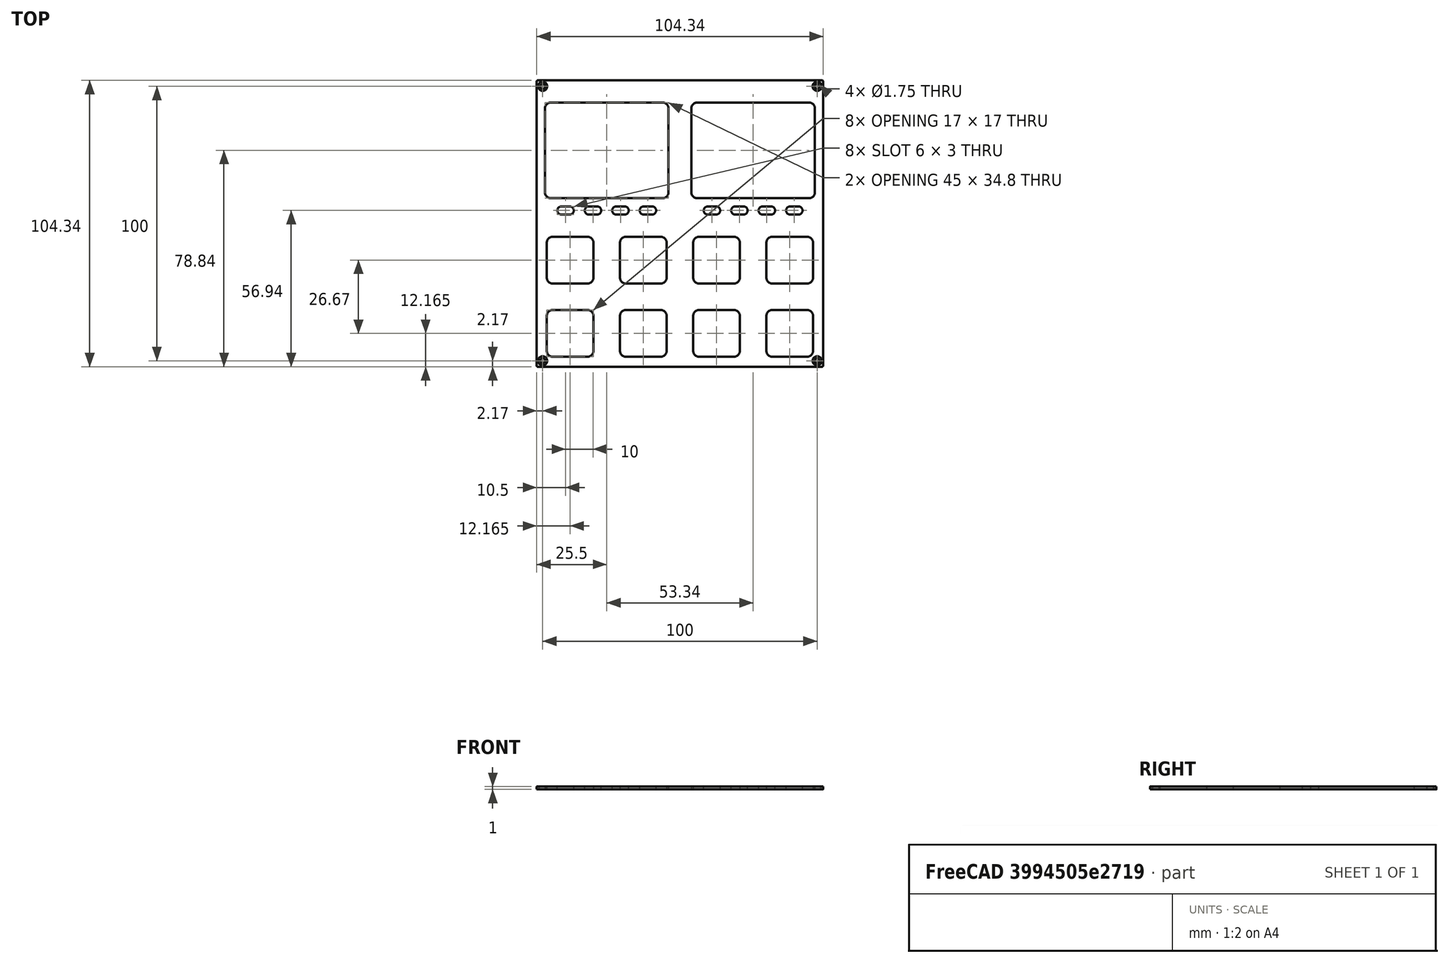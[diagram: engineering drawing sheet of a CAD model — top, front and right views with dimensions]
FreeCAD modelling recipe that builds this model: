
FCSTD DOCUMENT  (FreeCAD 1.0R39109 (Git))
Label: FRONTPANEL-SHEET-VSN2 - button_version1
License: All rights reserved
LicenseURL: https://en.wikipedia.org/wiki/All_rights_reserved
objects: TechDraw::DrawViewDimension×14, Sketcher::SketchObject×11, TechDraw::DrawViewBalloon×11, TechDraw::DrawHatch×11, TechDraw::DrawViewAnnotation×6, TechDraw::DrawViewPart×5, PartDesign::Pocket×4, TechDraw::DrawSVGTemplate×2, PartDesign::Body×2, TechDraw::DrawPage×2, Spreadsheet::Sheet×1, PartDesign::Pad×1, PartDesign::Hole×1, PartDesign::FeatureBase×1, TechDraw::DrawComplexSection×1
note: 65 computed .brp shape members not serialized (recipe doc carries the construction recipe); baked Part::Feature solids carry a one-line shape summary decoded from their .brp

FEATURE [TechDraw::DrawSVGTemplate] Template
  EditableTexts = COLOR=Anodized matte black - RAL code: 9004; CreationDate=2024/08/29; E.G.APPROVED=PRELIMINARY; FC-Scale=1:1; FC-Title=VSN2 - frontpanel; IntechStudioLtd.=Intech Studio Ltd.; MATERIAL=Aluminum 5052-H32; REV=01; STANDARD=ISO 2768 - m
  Height = 297
  Orientation = 1
  Template = <userpath>/Desktop/A3_LandscapeTD_MODIFIED.svg
  Width = 420
FEATURE [Spreadsheet::Sheet] Spreadsheet  label="dim"
  cells = A1='panel_length; B1(panel_length)=104.35; A2='panel_thickness; B2(panel_thickness)=1; A3='panel_radius; B3(panel_radius)==(104.35 - 103.6) / 2; A5='corner_drill_dist; B5(corner_drill_dist)=100; A6='corner_drill_dia; B6(corner_drill_dia)=1.75; A7='corner_drill_countersink; B7(corner_drill_countersink)=3.3; A9='undercut_width; B9(undercut_width)=1; A10='undercut_length; B10(undercut_length)=90; A11='undercut_offset; B11(undercut_offset)=1; A12='undercut_depth; B12(undercut_depth)=0.8; A14='ui_raster; B14(ui_raster)=26.67; A16='light_drill_dia; B16(light_drill_dia)=3; D16='old 2.9; A17='light_bore_dia; B17(light_bore_dia)=3.45; C17='check; D17='old 3.30; E17='DEPRICATED; A18='light_bore_depth; B18(light_bore_depth)=0.4; C18='check; D18='old 0.40; E18='DEPRICATED; A20='pot_drill_dia; B20(pot_drill_dia)=9.8; C20='check; D20='old 6.20; A21='pot_led_dist; B21(pot_led_dist)=8.5; B22=0; A23='but_drill_dia; B23(but_drill_dia)=9.8; A24='but_led_dist; B24(but_led_dist)=8.5; A26='fad_cutout_width; B26(fad_cutout_width)=2.1; C26='check; D26='old 1.50; A27='fad_cutout_length; B27(fad_cutout_length)=36; A28='fad_led_dist; B28(fad_led_dist)=25; A30='enc_drill_dia; B30(enc_drill_dia)=9.8; C30='check; D30='old 6.20; A31='enc_led_dist; B31(enc_led_dist)=8.5; A33='longfad_cutout_width; B33(longfad_cutout_width)=2.1; A34='longfad_cutout_length; B34(longfad_cutout_length)=66; A36='panel_chamfer; B36(panel_chamfer)=0.2; C36='UPDATE DRAWING
FEATURE [Sketcher::SketchObject] Sketch025  label="TEK2_TEKLight"
  ArcFitTolerance = 0
  AttachmentSupport = -> [XY_Plane011]
  FullyConstrained = true
  MakeInternals = false
  MapMode = 5
  expr: Constraints[49] = <<dim>>.light_drill_dia
  sketch-geometry (28):
    g0: Circle [constr] CenterX=-26.67 CenterY=26.67 CenterZ=0 NormalX=0 NormalY=0 NormalZ=1 AngleXU=0 Radius=5.25
    g1: Circle CenterX=26.67 CenterY=26.67 CenterZ=0 NormalX=0 NormalY=0 NormalZ=1 AngleXU=0 Radius=5.25
    g2: LineSegment [constr] StartX=-26.67 StartY=26.67 StartZ=0 EndX=0 EndY=26.67 EndZ=0
    g3: LineSegment [constr] StartX=0 StartY=26.67 StartZ=0 EndX=0 EndY=0 EndZ=0
    g4: LineSegment [constr] StartX=26.67 StartY=26.67 StartZ=0 EndX=0 EndY=26.67 EndZ=0
    g5: Circle [constr] CenterX=-26.67 CenterY=26.67 CenterZ=0 NormalX=0 NormalY=0 NormalZ=1 AngleXU=0 Radius=23
    g6: Circle [constr] CenterX=26.67 CenterY=26.67 CenterZ=0 NormalX=0 NormalY=0 NormalZ=1 AngleXU=0 Radius=23
    g7: Circle [constr] CenterX=-47.5151 CenterY=36.3902 CenterZ=0 NormalX=0 NormalY=0 NormalZ=1 AngleXU=0 Radius=1.5
    g8: Circle [constr] CenterX=-45.5105 CenterY=39.8623 CenterZ=0 NormalX=0 NormalY=0 NormalZ=1 AngleXU=0 Radius=1.5
    g9: Circle [constr] CenterX=-42.9335 CenterY=42.9335 CenterZ=0 NormalX=0 NormalY=0 NormalZ=1 AngleXU=0 Radius=1.5
    g10: Circle [constr] CenterX=-39.8623 CenterY=45.5105 CenterZ=0 NormalX=0 NormalY=0 NormalZ=1 AngleXU=0 Radius=1.5
    g11: Circle [constr] CenterX=-36.3902 CenterY=47.5151 CenterZ=0 NormalX=0 NormalY=0 NormalZ=1 AngleXU=0 Radius=1.5
    g12: Circle CenterX=5.82492 CenterY=36.3902 CenterZ=0 NormalX=0 NormalY=0 NormalZ=1 AngleXU=0 Radius=1.5
    g13: Circle CenterX=7.8295 CenterY=39.8623 CenterZ=0 NormalX=0 NormalY=0 NormalZ=1 AngleXU=0 Radius=1.5
    g14: Circle CenterX=10.4065 CenterY=42.9335 CenterZ=0 NormalX=0 NormalY=0 NormalZ=1 AngleXU=0 Radius=1.5
    g15: Circle CenterX=13.4777 CenterY=45.5105 CenterZ=0 NormalX=0 NormalY=0 NormalZ=1 AngleXU=0 Radius=1.5
    g16: Circle CenterX=16.9498 CenterY=47.5151 CenterZ=0 NormalX=0 NormalY=0 NormalZ=1 AngleXU=0 Radius=1.5
    g17: LineSegment [constr] StartX=-47.5151 StartY=36.3902 StartZ=0 EndX=5.82492 EndY=36.3902 EndZ=0
    g18: LineSegment [constr] StartX=-45.5105 StartY=39.8623 StartZ=0 EndX=7.8295 EndY=39.8623 EndZ=0
    g19: LineSegment [constr] StartX=-42.9335 StartY=42.9335 StartZ=0 EndX=10.4065 EndY=42.9335 EndZ=0
    g20: LineSegment [constr] StartX=-39.8623 StartY=45.5105 StartZ=0 EndX=13.4777 EndY=45.5105 EndZ=0
    g21: LineSegment [constr] StartX=-36.3902 StartY=47.5151 StartZ=0 EndX=16.9498 EndY=47.5151 EndZ=0
    g22: LineSegment [constr] StartX=5.82492 StartY=36.3902 StartZ=0 EndX=26.67 EndY=26.67 EndZ=0
    g23: LineSegment [constr] StartX=16.9498 StartY=47.5151 StartZ=0 EndX=26.67 EndY=26.67 EndZ=0
    g24: LineSegment [constr] StartX=5.82492 StartY=36.3902 StartZ=0 EndX=7.8295 EndY=39.8623 EndZ=0
    g25: LineSegment [constr] StartX=7.8295 StartY=39.8623 StartZ=0 EndX=10.4065 EndY=42.9335 EndZ=0
    g26: LineSegment [constr] StartX=13.4777 StartY=45.5105 StartZ=0 EndX=10.4065 EndY=42.9335 EndZ=0
    g27: LineSegment [constr] StartX=16.9498 StartY=47.5151 StartZ=0 EndX=13.4777 EndY=45.5105 EndZ=0
  constraints (69):
    c: Coincident(g2,g0)
    c: PointOnObject(g2,g-2)
    c: Coincident(g2,g3)
    c: Coincident(g3,g-1)
    c: Coincident(g4,g1)
    c: Coincident(g4,g2)
    c: Equal(g3,g2)
    c: Equal(g2,g4)
    c: Horizontal(g2)
    c: Horizontal(g4)
    c: DistanceY(g3,g3) = 26.67
    c: Equal(g0,g1)
    c: Coincident(g5,g0)
    c: Coincident(g6,g1)
    c: Equal(g6,g5)
    c: PointOnObject(g7,g5)
    c: PointOnObject(g8,g5)
    c: PointOnObject(g9,g5)
    c: PointOnObject(g10,g5)
    c: PointOnObject(g11,g5)
    c: PointOnObject(g12,g6)
    c: PointOnObject(g13,g6)
    c: PointOnObject(g14,g6)
    c: PointOnObject(g15,g6)
    c: PointOnObject(g16,g6)
    c: Equal(g7,g8)
    c: Equal(g8,g9)
    c: Equal(g9,g10)
    c: Equal(g10,g11)
    c: Equal(g11,g12)
    c: Equal(g12,g13)
    c: Equal(g13,g14)
    c: Equal(g14,g15)
    c: Equal(g15,g16)
    c: Coincident(g17,g7)
    c: Coincident(g17,g12)
    c: Coincident(g18,g8)
    c: Coincident(g18,g13)
    c: Horizontal(g18)
    c: Coincident(g19,g9)
    c: Coincident(g19,g14)
    c: Horizontal(g19)
    c: Coincident(g20,g10)
    c: Coincident(g20,g15)
    c: Horizontal(g20)
    c: Coincident(g21,g11)
    c: Horizontal(g21)
    c: Coincident(g21,g16)
    c: Horizontal(g17)
    c: Diameter(g12) = 3
    c: Coincident(g22,g12)
    c: Coincident(g22,g1)
    c: Coincident(g23,g16)
    c: Coincident(g23,g1)
    c: Angle(g22,g4) = 0.436332
    c: Angle(g-2,g23) = 0.436332
    c: Coincident(g24,g12)
    c: Coincident(g24,g13)
    c: Coincident(g25,g13)
    c: Coincident(g26,g15)
    c: Coincident(g26,g25)
    c: Coincident(g27,g16)
    c: Coincident(g27,g15)
    c: Coincident(g25,g14)
    c: Equal(g24,g25)
    c: Equal(g25,g26)
    c: Equal(g26,g27)
    c: Radius(g6) = 23
    c: Diameter(g1) = 10.5
FEATURE [Sketcher::SketchObject] Sketch024  label="TEK2_ButtonLight"
  ArcFitTolerance = 0
  AttachmentSupport = -> [XY_Plane011]
  FullyConstrained = true
  MakeInternals = false
  MapMode = 5
  expr: Constraints[42] = <<dim>>.but_led_dist
  sketch-geometry (17):
    g0: Circle CenterX=-40.005 CenterY=-4.835 CenterZ=0 NormalX=0 NormalY=0 NormalZ=1 AngleXU=0 Radius=2
    g1: Circle CenterX=-13.335 CenterY=-4.835 CenterZ=0 NormalX=0 NormalY=0 NormalZ=1 AngleXU=0 Radius=2
    g2: LineSegment [constr] StartX=-40.005 StartY=-4.835 StartZ=0 EndX=-13.335 EndY=-4.835 EndZ=0
    g3: Circle CenterX=13.335 CenterY=-4.835 CenterZ=0 NormalX=0 NormalY=0 NormalZ=1 AngleXU=0 Radius=2
    g4: LineSegment [constr] StartX=-13.335 StartY=-4.835 StartZ=0 EndX=13.335 EndY=-4.835 EndZ=0
    g5: Circle CenterX=40.005 CenterY=-4.835 CenterZ=0 NormalX=0 NormalY=0 NormalZ=1 AngleXU=0 Radius=2
    g6: LineSegment [constr] StartX=13.335 StartY=-4.835 StartZ=0 EndX=40.005 EndY=-4.835 EndZ=0
    g7: Circle CenterX=-40.005 CenterY=-31.505 CenterZ=0 NormalX=0 NormalY=0 NormalZ=1 AngleXU=0 Radius=2
    g8: LineSegment [constr] StartX=-40.005 StartY=-4.835 StartZ=0 EndX=-40.005 EndY=-31.505 EndZ=0
    g9: Circle CenterX=-13.335 CenterY=-31.505 CenterZ=0 NormalX=0 NormalY=0 NormalZ=1 AngleXU=0 Radius=2
    g10: LineSegment [constr] StartX=-40.005 StartY=-31.505 StartZ=0 EndX=-13.335 EndY=-31.505 EndZ=0
    g11: Circle CenterX=13.335 CenterY=-31.505 CenterZ=0 NormalX=0 NormalY=0 NormalZ=1 AngleXU=0 Radius=2
    g12: LineSegment [constr] StartX=-13.335 StartY=-31.505 StartZ=0 EndX=13.335 EndY=-31.505 EndZ=0
    g13: Circle CenterX=40.005 CenterY=-31.505 CenterZ=0 NormalX=0 NormalY=0 NormalZ=1 AngleXU=0 Radius=2
    g14: LineSegment [constr] StartX=13.335 StartY=-31.505 StartZ=0 EndX=40.005 EndY=-31.505 EndZ=0
    g15: LineSegment [constr] StartX=-13.335 StartY=-4.835 StartZ=0 EndX=-1.8e-15 EndY=8.5 EndZ=0
    g16: LineSegment [constr] StartX=-1.8e-15 StartY=8.5 StartZ=0 EndX=13.335 EndY=-4.835 EndZ=0
  constraints (43):
    c: Diameter(g0) = 4
    c: Coincident(g0,g2)
    c: Coincident(g1,g2)
    c: Coincident(g1,g4)
    c: Coincident(g3,g4)
    c: Coincident(g3,g6)
    c: Coincident(g5,g6)
    c: Coincident(g0,g8)
    c: Coincident(g7,g8)
    c: Coincident(g7,g10)
    c: Coincident(g9,g10)
    c: Coincident(g9,g12)
    c: Coincident(g11,g12)
    c: Coincident(g11,g14)
    c: Coincident(g13,g14)
    c: Horizontal(g4)
    c: Horizontal(g2)
    c: Horizontal(g6)
    c: Horizontal(g10)
    c: Horizontal(g12)
    c: Horizontal(g14)
    c: Vertical(g8)
    c: Equal(g8,g2)
    c: Equal(g2,g10)
    c: Equal(g10,g12)
    c: Equal(g12,g4)
    c: Equal(g4,g6)
    c: Equal(g6,g14)
    c: DistanceX(g4,g4) = 26.67
    c: Equal(g7,g9)
    c: Equal(g9,g11)
    c: Equal(g11,g13)
    c: Equal(g13,g5)
    c: Equal(g5,g3)
    c: Equal(g3,g1)
    c: Equal(g1,g0)
    c: Coincident(g15,g1)
    c: PointOnObject(g15,g-2)
    c: Coincident(g15,g16)
    c: Coincident(g16,g3)
    c: Equal(g16,g15)
    c: Perpendicular(g15,g16)
    c: DistanceY(g-1,g15) = 8.5
FEATURE [Sketcher::SketchObject] Sketch023  label="TEK2_ButtonHole"
  ArcFitTolerance = 0
  AttachmentSupport = -> [XY_Plane011]
  FullyConstrained = true
  MakeInternals = false
  MapMode = 5
  sketch-geometry (17):
    g0: Circle CenterX=-40.005 CenterY=-13.335 CenterZ=0 NormalX=0 NormalY=0 NormalZ=1 AngleXU=0 Radius=2
    g1: Circle CenterX=-13.335 CenterY=-13.335 CenterZ=0 NormalX=0 NormalY=0 NormalZ=1 AngleXU=0 Radius=2
    g2: LineSegment [constr] StartX=-40.005 StartY=-13.335 StartZ=0 EndX=-13.335 EndY=-13.335 EndZ=0
    g3: Circle CenterX=13.335 CenterY=-13.335 CenterZ=0 NormalX=0 NormalY=0 NormalZ=1 AngleXU=0 Radius=2
    g4: LineSegment [constr] StartX=-13.335 StartY=-13.335 StartZ=0 EndX=13.335 EndY=-13.335 EndZ=0
    g5: Circle CenterX=40.005 CenterY=-13.335 CenterZ=0 NormalX=0 NormalY=0 NormalZ=1 AngleXU=0 Radius=2
    g6: LineSegment [constr] StartX=13.335 StartY=-13.335 StartZ=0 EndX=40.005 EndY=-13.335 EndZ=0
    g7: Circle CenterX=-40.005 CenterY=-40.005 CenterZ=0 NormalX=0 NormalY=0 NormalZ=1 AngleXU=0 Radius=2
    g8: LineSegment [constr] StartX=-40.005 StartY=-13.335 StartZ=0 EndX=-40.005 EndY=-40.005 EndZ=0
    g9: Circle CenterX=-13.335 CenterY=-40.005 CenterZ=0 NormalX=0 NormalY=0 NormalZ=1 AngleXU=0 Radius=2
    g10: LineSegment [constr] StartX=-40.005 StartY=-40.005 StartZ=0 EndX=-13.335 EndY=-40.005 EndZ=0
    g11: Circle CenterX=13.335 CenterY=-40.005 CenterZ=0 NormalX=0 NormalY=0 NormalZ=1 AngleXU=0 Radius=2
    g12: LineSegment [constr] StartX=-13.335 StartY=-40.005 StartZ=0 EndX=13.335 EndY=-40.005 EndZ=0
    g13: Circle CenterX=40.005 CenterY=-40.005 CenterZ=0 NormalX=0 NormalY=0 NormalZ=1 AngleXU=0 Radius=2
    g14: LineSegment [constr] StartX=13.335 StartY=-40.005 StartZ=0 EndX=40.005 EndY=-40.005 EndZ=0
    g15: LineSegment [constr] StartX=0 StartY=0 StartZ=0 EndX=13.335 EndY=-13.335 EndZ=0
    g16: LineSegment [constr] StartX=0 StartY=0 StartZ=0 EndX=-13.335 EndY=-13.335 EndZ=0
  constraints (42):
    c: Diameter(g0) = 4
    c: Coincident(g0,g2)
    c: Coincident(g1,g2)
    c: Coincident(g1,g4)
    c: Coincident(g3,g4)
    c: Coincident(g3,g6)
    c: Coincident(g5,g6)
    c: Coincident(g0,g8)
    c: Coincident(g7,g8)
    c: Coincident(g7,g10)
    c: Coincident(g9,g10)
    c: Coincident(g9,g12)
    c: Coincident(g11,g12)
    c: Coincident(g11,g14)
    c: Coincident(g13,g14)
    c: Coincident(g-1,g16)
    c: Coincident(g16,g1)
    c: Coincident(g15,g3)
    c: Horizontal(g4)
    c: Horizontal(g2)
    c: Horizontal(g6)
    c: Horizontal(g10)
    c: Horizontal(g12)
    c: Horizontal(g14)
    c: Vertical(g8)
    c: Equal(g8,g2)
    c: Equal(g2,g10)
    c: Equal(g10,g12)
    c: Equal(g12,g4)
    c: Equal(g4,g6)
    c: Equal(g6,g14)
    c: DistanceX(g4,g4) = 26.67
    c: Equal(g16,g15)
    c: Coincident(g15,g16)
    c: Perpendicular(g15,g16)
    c: Equal(g7,g9)
    c: Equal(g9,g11)
    c: Equal(g11,g13)
    c: Equal(g13,g5)
    c: Equal(g5,g3)
    c: Equal(g3,g1)
    c: Equal(g1,g0)
FEATURE [Sketcher::SketchObject] Sketch001
  ArcFitTolerance = 0
  AttachmentSupport = -> [XY_Plane]
  FullyConstrained = true
  MakeInternals = false
  MapMode = 5
  expr: Constraints[13] = <<dim>>.corner_drill_dist
  sketch-geometry (9):
    g0: LineSegment [constr] StartX=-50 StartY=50 StartZ=0 EndX=-50 EndY=-50 EndZ=0
    g1: LineSegment [constr] StartX=-50 StartY=-50 StartZ=0 EndX=50 EndY=-50 EndZ=0
    g2: LineSegment [constr] StartX=50 StartY=-50 StartZ=0 EndX=50 EndY=50 EndZ=0
    g3: LineSegment [constr] StartX=50 StartY=50 StartZ=0 EndX=-50 EndY=50 EndZ=0
    g4: Circle [constr] CenterX=0 CenterY=0 CenterZ=0 NormalX=0 NormalY=0 NormalZ=1 AngleXU=0 Radius=70.7107
    g5: Circle CenterX=-50 CenterY=50 CenterZ=0 NormalX=0 NormalY=0 NormalZ=1 AngleXU=0 Radius=0.5
    g6: Circle CenterX=50 CenterY=50 CenterZ=0 NormalX=0 NormalY=0 NormalZ=1 AngleXU=0 Radius=0.5
    g7: Circle CenterX=50 CenterY=-50 CenterZ=0 NormalX=0 NormalY=0 NormalZ=1 AngleXU=0 Radius=0.5
    g8: Circle CenterX=-50 CenterY=-50 CenterZ=0 NormalX=0 NormalY=0 NormalZ=1 AngleXU=0 Radius=0.5
  constraints (22):
    c: Coincident(g0,g1)
    c: Coincident(g1,g2)
    c: Coincident(g2,g3)
    c: Coincident(g3,g0)
    c: Equal(g0,g1)
    c: Equal(g0,g2)
    c: Equal(g0,g3)
    c: PointOnObject(g0,g4)
    c: PointOnObject(g1,g4)
    c: PointOnObject(g2,g4)
    c: PointOnObject(g3,g4)
    c: Coincident(g4,g-1)
    c: Horizontal(g3)
    c: DistanceX(g3,g3) = 100
    c: Coincident(g5,g0)
    c: Coincident(g6,g2)
    c: Coincident(g7,g1)
    c: Coincident(g8,g0)
    c: Diameter(g8) = 1
    c: Equal(g8,g7)
    c: Equal(g8,g6)
    c: Equal(g8,g5)
FEATURE [Sketcher::SketchObject] Sketch002
  ArcFitTolerance = 0
  AttachmentOffset = pos=(0,0,-4.8) rot=(0,0,1;0rad)
  AttachmentSupport = -> [XY_Plane]
  FullyConstrained = true
  MakeInternals = false
  MapMode = 5
  Placement = pos=(0,0,-4.8) rot=(0,0,1;0rad)
  expr: .AttachmentOffset.Base.z = -<<dim>>.undercut_depth - 4
  expr: Constraints[91] = <<dim>>.undercut_length
  expr: Constraints[92] = <<dim>>.undercut_width
  expr: Constraints[93] = <<dim>>.panel_length / 2 - <<dim>>.undercut_offset - <<dim>>.undercut_width / 2
  sketch-geometry (40):
    g0: LineSegment StartX=-45 StartY=50.175 StartZ=0 EndX=45 EndY=50.175 EndZ=0
    g1: LineSegment StartX=-45 StartY=51.175 StartZ=0 EndX=45 EndY=51.175 EndZ=0
    g2: LineSegment [constr] StartX=-50.675 StartY=45 StartZ=0 EndX=0 EndY=0 EndZ=0
    g3: LineSegment [constr] StartX=0 StartY=0 StartZ=0 EndX=-50.675 EndY=-45 EndZ=0
    g4: LineSegment [constr] StartX=0 StartY=0 StartZ=0 EndX=-45 EndY=50.675 EndZ=0
    g5: LineSegment [constr] StartX=45 StartY=50.675 StartZ=0 EndX=0 EndY=0 EndZ=0
    g6: LineSegment [constr] StartX=0 StartY=0 StartZ=0 EndX=50.675 EndY=45 EndZ=0
    g7: LineSegment [constr] StartX=50.675 StartY=-45 StartZ=0 EndX=0 EndY=0 EndZ=0
    g8: LineSegment [constr] StartX=0 StartY=0 StartZ=0 EndX=45 EndY=-50.675 EndZ=0
    g9: LineSegment [constr] StartX=0 StartY=0 StartZ=0 EndX=-45 EndY=-50.675 EndZ=0
    g10: ArcOfCircle CenterX=45 CenterY=50.675 CenterZ=0 NormalX=0 NormalY=0 NormalZ=1 AngleXU=0 Radius=0.5 StartAngle=4.71239 EndAngle=6.28319
    g11: ArcOfCircle CenterX=45 CenterY=50.675 CenterZ=0 NormalX=0 NormalY=0 NormalZ=1 AngleXU=0 Radius=0.5 StartAngle=0 EndAngle=1.5708
    g12: LineSegment [constr] StartX=45 StartY=50.675 StartZ=0 EndX=45.5 EndY=50.675 EndZ=0
    g13: ArcOfCircle CenterX=-45 CenterY=50.675 CenterZ=0 NormalX=0 NormalY=0 NormalZ=1 AngleXU=0 Radius=0.5 StartAngle=3.14159 EndAngle=4.71239
    g14: ArcOfCircle CenterX=-45 CenterY=50.675 CenterZ=0 NormalX=0 NormalY=0 NormalZ=1 AngleXU=0 Radius=0.5 StartAngle=1.5708 EndAngle=3.14159
    g15: LineSegment [constr] StartX=-45.5 StartY=50.675 StartZ=0 EndX=-45 EndY=50.675 EndZ=0
    g16: LineSegment StartX=-45 StartY=-51.175 StartZ=0 EndX=45 EndY=-51.175 EndZ=0
    g17: LineSegment StartX=-45 StartY=-50.175 StartZ=0 EndX=45 EndY=-50.175 EndZ=0
    g18: ArcOfCircle CenterX=45 CenterY=-50.675 CenterZ=0 NormalX=0 NormalY=0 NormalZ=1 AngleXU=0 Radius=0.5 StartAngle=4.71239 EndAngle=6.28319
    g19: ArcOfCircle CenterX=45 CenterY=-50.675 CenterZ=0 NormalX=0 NormalY=0 NormalZ=1 AngleXU=0 Radius=0.5 StartAngle=0 EndAngle=1.5708
    g20: LineSegment [constr] StartX=45 StartY=-50.675 StartZ=0 EndX=45.5 EndY=-50.675 EndZ=0
    g21: ArcOfCircle CenterX=-45 CenterY=-50.675 CenterZ=0 NormalX=0 NormalY=0 NormalZ=1 AngleXU=0 Radius=0.5 StartAngle=3.14159 EndAngle=4.71239
    g22: ArcOfCircle CenterX=-45 CenterY=-50.675 CenterZ=0 NormalX=0 NormalY=0 NormalZ=1 AngleXU=0 Radius=0.5 StartAngle=1.5708 EndAngle=3.14159
    g23: LineSegment [constr] StartX=-45.5 StartY=-50.675 StartZ=0 EndX=-45 EndY=-50.675 EndZ=0
    g24: LineSegment StartX=51.175 StartY=-45 StartZ=0 EndX=51.175 EndY=45 EndZ=0
    g25: LineSegment StartX=50.175 StartY=-45 StartZ=0 EndX=50.175 EndY=45 EndZ=0
    g26: ArcOfCircle CenterX=50.675 CenterY=45 CenterZ=0 NormalX=0 NormalY=0 NormalZ=1 AngleXU=0 Radius=0.5 StartAngle=3.8e-15 EndAngle=1.5708
    g27: ArcOfCircle CenterX=50.675 CenterY=45 CenterZ=0 NormalX=0 NormalY=0 NormalZ=1 AngleXU=0 Radius=0.5 StartAngle=1.5708 EndAngle=3.14159
    g28: LineSegment [constr] StartX=50.675 StartY=45 StartZ=0 EndX=50.675 EndY=45.5 EndZ=0
    g29: ArcOfCircle CenterX=50.675 CenterY=-45 CenterZ=0 NormalX=0 NormalY=0 NormalZ=1 AngleXU=0 Radius=0.5 StartAngle=4.71239 EndAngle=6.28319
    g30: ArcOfCircle CenterX=50.675 CenterY=-45 CenterZ=0 NormalX=0 NormalY=0 NormalZ=1 AngleXU=0 Radius=0.5 StartAngle=3.14159 EndAngle=4.71239
    g31: LineSegment [constr] StartX=50.675 StartY=-45.5 StartZ=0 EndX=50.675 EndY=-45 EndZ=0
    g32: LineSegment StartX=-50.175 StartY=-45 StartZ=0 EndX=-50.175 EndY=45 EndZ=0
    g33: LineSegment StartX=-51.175 StartY=-45 StartZ=0 EndX=-51.175 EndY=45 EndZ=0
    g34: ArcOfCircle CenterX=-50.675 CenterY=45 CenterZ=0 NormalX=0 NormalY=0 NormalZ=1 AngleXU=0 Radius=0.5 StartAngle=1.4e-15 EndAngle=1.5708
    g35: ArcOfCircle CenterX=-50.675 CenterY=45 CenterZ=0 NormalX=0 NormalY=0 NormalZ=1 AngleXU=0 Radius=0.5 StartAngle=1.5708 EndAngle=3.14159
    g36: LineSegment [constr] StartX=-50.675 StartY=45 StartZ=0 EndX=-50.675 EndY=45.5 EndZ=0
    g37: ArcOfCircle CenterX=-50.675 CenterY=-45 CenterZ=0 NormalX=0 NormalY=0 NormalZ=1 AngleXU=0 Radius=0.5 StartAngle=4.71239 EndAngle=6.28319
    g38: ArcOfCircle CenterX=-50.675 CenterY=-45 CenterZ=0 NormalX=0 NormalY=0 NormalZ=1 AngleXU=0 Radius=0.5 StartAngle=3.14159 EndAngle=4.71239
    g39: LineSegment [constr] StartX=-50.675 StartY=-45.5 StartZ=0 EndX=-50.675 EndY=-45 EndZ=0
  constraints (96):
    c: Horizontal(g0)
    c: Coincident(g2,g-1)
    c: Coincident(g2,g3)
    c: Coincident(g-1,g4)
    c: Coincident(g5,g-1)
    c: Coincident(g5,g6)
    c: Coincident(g7,g-1)
    c: Coincident(g7,g8)
    c: Coincident(g-1,g9)
    c: Equal(g5,g6)
    c: Equal(g6,g8)
    c: Equal(g8,g7)
    c: Equal(g7,g9)
    c: Equal(g9,g3)
    c: Equal(g3,g2)
    c: Equal(g2,g4)
    c: Coincident(g10,g5)
    c: Coincident(g11,g10)
    c: Coincident(g11,g10)
    c: Tangent(g11,g1) = 1.5708
    c: Tangent(g10,g0) = -1.5708
    c: Coincident(g12,g10)
    c: Coincident(g12,g10)
    c: Horizontal(g12)
    c: Coincident(g13,g4)
    c: Coincident(g14,g13)
    c: Coincident(g14,g13)
    c: Tangent(g14,g1) = 1.5708
    c: Tangent(g13,g0) = -1.5708
    c: Coincident(g15,g13)
    c: Coincident(g15,g13)
    c: Horizontal(g15)
    c: Horizontal(g1)
    c: Horizontal(g16)
    c: Coincident(g19,g18)
    c: Coincident(g19,g18)
    c: Tangent(g19,g17) = 1.5708
    c: Tangent(g18,g16) = -1.5708
    c: Coincident(g20,g18)
    c: Coincident(g20,g18)
    c: Horizontal(g20)
    c: Coincident(g22,g21)
    c: Coincident(g22,g21)
    c: Tangent(g22,g17) = 1.5708
    c: Tangent(g21,g16) = -1.5708
    c: Coincident(g23,g21)
    c: Coincident(g23,g21)
    c: Horizontal(g23)
    c: Horizontal(g17)
    c: Coincident(g21,g9)
    c: Coincident(g8,g18)
    c: Equal(g22,g14)
    c: Equal(g17,g1)
    c: Coincident(g27,g26)
    c: Coincident(g27,g26)
    c: Tangent(g27,g25) = 1.5708
    c: Tangent(g26,g24) = -1.5708
    c: Coincident(g28,g26)
    c: Coincident(g28,g26)
    c: Coincident(g30,g29)
    c: Coincident(g30,g29)
    c: Tangent(g30,g25) = 1.5708
    c: Tangent(g29,g24) = -1.5708
    c: Coincident(g31,g29)
    c: Coincident(g31,g29)
    c: Vertical(g31)
    c: Vertical(g28)
    c: Vertical(g25)
    c: Vertical(g24)
    c: Coincident(g35,g34)
    c: Coincident(g35,g34)
    c: Tangent(g35,g33) = 1.5708
    c: Tangent(g34,g32) = -1.5708
    c: Coincident(g36,g34)
    c: Coincident(g36,g34)
    c: Coincident(g38,g37)
    c: Coincident(g38,g37)
    c: Tangent(g38,g33) = 1.5708
    c: Tangent(g37,g32) = -1.5708
    c: Coincident(g39,g37)
    c: Coincident(g39,g37)
    c: Vertical(g39)
    c: Vertical(g36)
    c: Vertical(g33)
    c: Vertical(g32)
    c: Coincident(g6,g26)
    c: Coincident(g7,g29)
    c: Equal(g25,g0)
    c: Equal(g11,g27)
    c: Equal(g1,g33)
    c: Equal(g35,g11)
    c: DistanceX(g13,g10) = 90
    c: Diameter(g13) = 1
    c: DistanceY(g-1,g13) = 50.675
    c: Coincident(g2,g34)
    c: Coincident(g3,g37)
FEATURE [Sketcher::SketchObject] Sketch
  ArcFitTolerance = 0
  AttachmentSupport = -> [XY_Plane]
  FullyConstrained = true
  MakeInternals = false
  MapMode = 5
  expr: Constraints[12] = <<dim>>.panel_radius
  expr: Constraints[16] = <<dim>>.panel_length
  sketch-geometry (11):
    g0: LineSegment StartX=-51.8 StartY=52.175 StartZ=0 EndX=51.8 EndY=52.175 EndZ=0
    g1: LineSegment StartX=52.175 StartY=51.8 StartZ=0 EndX=52.175 EndY=-51.8 EndZ=0
    g2: LineSegment StartX=51.8 StartY=-52.175 StartZ=0 EndX=-51.8 EndY=-52.175 EndZ=0
    g3: LineSegment StartX=-52.175 StartY=-51.8 StartZ=0 EndX=-52.175 EndY=51.8 EndZ=0
    g4: ArcOfCircle CenterX=-51.8 CenterY=51.8 CenterZ=0 NormalX=0 NormalY=0 NormalZ=1 AngleXU=0 Radius=0.375 StartAngle=1.5708 EndAngle=3.14159
    g5: ArcOfCircle CenterX=51.8 CenterY=51.8 CenterZ=0 NormalX=0 NormalY=0 NormalZ=1 AngleXU=0 Radius=0.375 StartAngle=8.4e-15 EndAngle=1.5708
    g6: ArcOfCircle CenterX=51.8 CenterY=-51.8 CenterZ=0 NormalX=0 NormalY=0 NormalZ=1 AngleXU=0 Radius=0.375 StartAngle=4.71239 EndAngle=6.28319
    g7: ArcOfCircle CenterX=-51.8 CenterY=-51.8 CenterZ=0 NormalX=0 NormalY=0 NormalZ=1 AngleXU=0 Radius=0.375 StartAngle=3.14159 EndAngle=4.71239
    g8: LineSegment [constr] StartX=-51.8 StartY=51.8 StartZ=0 EndX=0 EndY=0 EndZ=0
    g9: LineSegment [constr] StartX=0 StartY=0 StartZ=0 EndX=51.8 EndY=51.8 EndZ=0
    g10: LineSegment [constr] StartX=0 StartY=0 StartZ=0 EndX=-51.8 EndY=-51.8 EndZ=0
  constraints (26):
    c: Horizontal(g0)
    c: Horizontal(g2)
    c: Vertical(g1)
    c: Vertical(g3)
    c: Tangent(g3,g4) = 1.5708
    c: Tangent(g0,g4) = 1.5708
    c: Tangent(g0,g5) = 1.5708
    c: Tangent(g1,g5) = 1.5708
    c: Tangent(g1,g6) = 1.5708
    c: Tangent(g2,g6) = 1.5708
    c: Tangent(g2,g7) = 1.5708
    c: Tangent(g3,g7) = 1.5708
    c: Radius(g4) = 0.375
    c: Equal(g4,g5)
    c: Equal(g4,g6)
    c: Equal(g4,g7)
    c: DistanceX(g3,g1) = 104.35
    c: Equal(g3,g0)
    c: Coincident(g8,g4)
    c: Coincident(g8,g-1)
    c: Coincident(g8,g9)
    c: Coincident(g9,g5)
    c: Coincident(g-1,g10)
    c: Coincident(g10,g7)
    c: Equal(g10,g8)
    c: Equal(g8,g9)
FEATURE [PartDesign::Pad] Pad  label="panel"
  AllowMultiFace = false
  Direction = (0,0,1)
  Length = 1
  Length2 = 100
  Profile = -> Sketch
  Reversed = true
  Suppressed = false
  Type = 0
  expr: Length = <<dim>>.panel_thickness
FEATURE [PartDesign::Pocket] Pocket
  AllowMultiFace = false
  BaseFeature = -> Pad
  Direction = (0,0,-1)
  Length = 5
  Length2 = 100
  Profile = -> Sketch002
  Suppressed = false
  Type = 1
FEATURE [PartDesign::Hole] Hole
  BaseFeature = -> Pocket
  CustomThreadClearance = 0
  Depth = 298.105
  DepthType = 1
  Diameter = 1.75
  DrillForDepth = false
  DrillPoint = 1
  DrillPointAngle = 118
  HoleCutCountersinkAngle = 90
  HoleCutCustomValues = false
  HoleCutDepth = 0
  HoleCutDiameter = 3.3
  HoleCutType = 2
  ModelThread = false
  Profile = -> Sketch001
  Suppressed = false
  Tapered = false
  TaperedAngle = 90
  ThreadClass = 0
  ThreadDepth = 298.105
  ThreadDepthType = 0
  ThreadDirection = 0
  ThreadFit = 0
  ThreadSize = 0
  ThreadType = 0
  Threaded = false
  UseCustomThreadClearance = false
  expr: Diameter = <<dim>>.corner_drill_dia
  expr: HoleCutDiameter = <<dim>>.corner_drill_countersink
FEATURE [PartDesign::Body] Body  label="Base"
  AllowCompound = false
  Group = -> [Sketch,Pad,Sketch001,Sketch002,Pocket,Hole]
  Origin = -> Origin
  Tip = -> Hole
FEATURE [PartDesign::FeatureBase] Clone009
  BaseFeature = -> Body
  Suppressed = false
FEATURE [Sketcher::SketchObject] Sketch026  label="Section A-A"
  ArcFitTolerance = 0
  AttachmentSupport = -> [XY_Plane011]
  FullyConstrained = true
  MakeInternals = false
  MapMode = 5
  sketch-geometry (1):
    g0: LineSegment StartX=-53.5 StartY=-50 StartZ=0 EndX=-46.5 EndY=-50 EndZ=0
  constraints (4):
    c: Horizontal(g0)
    c: DistanceX(g0,g0) = 7
    c: DistanceY(g0,g-1) = 50
    c: DistanceX(g0,g-1) = 46.5
FEATURE [TechDraw::DrawViewAnnotation] Annotation
  Font = osifont
  LineSpace = 100
  LockPosition = false
  MaxWidth = -1
  Rotation = 0
  ScaleType = 0
  Text = 10:1
  TextSize = 4
  TextStyle = 0
  X = 287.429
  Y = 78.3445
FEATURE [TechDraw::DrawViewAnnotation] Annotation001
  Font = osifont
  LineSpace = 100
  LockPosition = false
  MaxWidth = -1
  Rotation = 0
  ScaleType = 0
  Text = 1:2
  TextSize = 4
  TextStyle = 0
  X = 191.608
  Y = 62.7873
FEATURE [Sketcher::SketchObject] Sketch027
  ArcFitTolerance = 0
  AttachmentSupport = -> [XY_Plane011]
  FullyConstrained = true
  MakeInternals = false
  MapMode = 5
  sketch-geometry (19):
    g0: LineSegment StartX=-49.17 StartY=11.27 StartZ=0 EndX=-49.17 EndY=42.07 EndZ=0
    g1: LineSegment StartX=-47.17 StartY=44.07 StartZ=0 EndX=-6.17 EndY=44.07 EndZ=0
    g2: LineSegment StartX=-4.17 StartY=42.07 StartZ=0 EndX=-4.17 EndY=11.27 EndZ=0
    g3: LineSegment StartX=-6.17 StartY=9.27 StartZ=0 EndX=-47.17 EndY=9.27 EndZ=0
    g4: GeomPoint [constr] X=-26.67 Y=26.67 Z=0
    g5: ArcOfCircle CenterX=-47.17 CenterY=42.07 CenterZ=0 NormalX=0 NormalY=0 NormalZ=1 AngleXU=0 Radius=2 StartAngle=1.5708 EndAngle=3.14159
    g6: ArcOfCircle CenterX=-6.17 CenterY=42.07 CenterZ=0 NormalX=0 NormalY=0 NormalZ=1 AngleXU=0 Radius=2 StartAngle=-1.8e-15 EndAngle=1.5708
    g7: ArcOfCircle CenterX=-6.17 CenterY=11.27 CenterZ=0 NormalX=0 NormalY=0 NormalZ=1 AngleXU=0 Radius=2 StartAngle=4.71239 EndAngle=6.28319
    g8: ArcOfCircle CenterX=-47.17 CenterY=11.27 CenterZ=0 NormalX=0 NormalY=0 NormalZ=1 AngleXU=0 Radius=2 StartAngle=3.14159 EndAngle=4.71239
    g9: LineSegment [constr] StartX=-26.67 StartY=44.07 StartZ=0 EndX=-26.67 EndY=9.27 EndZ=0
    g10: LineSegment [constr] StartX=-49.17 StartY=26.67 StartZ=0 EndX=-4.17 EndY=26.67 EndZ=0
    g11: LineSegment StartX=4.17 StartY=11.27 StartZ=0 EndX=4.17 EndY=42.07 EndZ=0
    g12: LineSegment StartX=6.17 StartY=44.07 StartZ=0 EndX=47.17 EndY=44.07 EndZ=0
    g13: LineSegment StartX=49.17 StartY=42.07 StartZ=0 EndX=49.17 EndY=11.27 EndZ=0
    g14: LineSegment StartX=47.17 StartY=9.27 StartZ=0 EndX=6.17 EndY=9.27 EndZ=0
    g15: ArcOfCircle CenterX=6.17 CenterY=42.07 CenterZ=0 NormalX=0 NormalY=0 NormalZ=1 AngleXU=0 Radius=2 StartAngle=1.5708 EndAngle=3.14159
    g16: ArcOfCircle CenterX=47.17 CenterY=42.07 CenterZ=0 NormalX=0 NormalY=0 NormalZ=1 AngleXU=0 Radius=2 StartAngle=-9e-16 EndAngle=1.5708
    g17: ArcOfCircle CenterX=47.17 CenterY=11.27 CenterZ=0 NormalX=0 NormalY=0 NormalZ=1 AngleXU=0 Radius=2 StartAngle=4.71239 EndAngle=6.28319
    g18: ArcOfCircle CenterX=6.17 CenterY=11.27 CenterZ=0 NormalX=0 NormalY=0 NormalZ=1 AngleXU=0 Radius=2 StartAngle=3.14159 EndAngle=4.71239
  constraints (48):
    c: Horizontal(g1)
    c: Horizontal(g3)
    c: Vertical(g0)
    c: Vertical(g2)
    c: DistanceY(g-1,g4) = 26.67
    c: Tangent(g1,g5) = 1.5708
    c: Tangent(g0,g5) = 1.5708
    c: Tangent(g1,g6) = 1.5708
    c: Tangent(g2,g6) = 1.5708
    c: Tangent(g2,g7) = 1.5708
    c: Tangent(g3,g7) = 1.5708
    c: Tangent(g3,g8) = 1.5708
    c: Tangent(g0,g8) = 1.5708
    c: Equal(g5,g6)
    c: Equal(g6,g7)
    c: Equal(g7,g8)
    c: DistanceX(g0,g2) = 45
    c: DistanceY(g3,g1) = 34.8
    c: PointOnObject(g9,g3)
    c: Vertical(g9)
    c: PointOnObject(g10,g0)
    c: Horizontal(g10)
    c: Symmetric(g2,g2,g10)
    c: Symmetric(g1,g1,g9)
    c: PointOnObject(g4,g9)
    c: PointOnObject(g4,g10)
    c: Diameter(g6) = 4
    c: DistanceX(g4,g-1) = 26.67
    c: DistanceY(g-1,g3) = 9.27
    c: Horizontal(g12)
    c: Horizontal(g14)
    c: Vertical(g11)
    c: Vertical(g13)
    c: Tangent(g12,g15) = 1.5708
    c: Tangent(g11,g15) = 1.5708
    c: Tangent(g12,g16) = 1.5708
    c: Tangent(g13,g16) = 1.5708
    c: Tangent(g13,g17) = 1.5708
    c: Tangent(g14,g17) = 1.5708
    c: Tangent(g11,g18) = 1.5708
    c: Tangent(g14,g18) = 1.5708
    c: Equal(g15,g16)
    c: Equal(g16,g17)
    c: Equal(g17,g18)
    c: Equal(g18,g7)
    c: Equal(g11,g2)
    c: Symmetric(g3,g14,g-2)
    c: Equal(g14,g3)
FEATURE [PartDesign::Pocket] Pocket008  label="TEK1_display"
  BaseFeature = -> Clone009
  Direction = (0,0,-1)
  Length = 5
  Length2 = 5
  Profile = -> Sketch027
  ReferenceAxis = -> Sketch027 [N_Axis]
  Suppressed = false
  Type = 1
FEATURE [Sketcher::SketchObject] Sketch028  label="LocatorPin"
  ArcFitTolerance = 0
  AttachmentSupport = -> [XY_Plane011]
  FullyConstrained = true
  MakeInternals = false
  MapMode = 5
  sketch-geometry (3):
    g0: Circle CenterX=-48.77 CenterY=8.17 CenterZ=0 NormalX=0 NormalY=0 NormalZ=1 AngleXU=0 Radius=0.6
    g1: Circle CenterX=-4.57 CenterY=45.17 CenterZ=0 NormalX=0 NormalY=0 NormalZ=1 AngleXU=0 Radius=0.6
    g2: GeomPoint [constr] X=-26.67 Y=26.67 Z=0
  constraints (8):
    c: Equal(g1,g0)
    c: Diameter(g1) = 1.2
    c: DistanceX(g2,g-1) = 26.67
    c: DistanceY(g-1,g2) = 26.67
    c: DistanceX(g0,g2) = 22.1
    c: DistanceY(g0,g2) = 18.5
    c: DistanceX(g2,g1) = 22.1
    c: DistanceY(g2,g1) = 18.5
FEATURE [Sketcher::SketchObject] Sketch029
  ArcFitTolerance = 0
  AttachmentSupport = -> [XY_Plane011]
  FullyConstrained = true
  MakeInternals = false
  MapMode = 5
  sketch-geometry (205):
    g0: LineSegment [constr] StartX=-47.07 StartY=4.77 StartZ=0 EndX=-6.27 EndY=4.77 EndZ=0
    g1: GeomPoint [constr] X=-26.67 Y=4.77 Z=0
    g2: LineSegment [constr] StartX=-34.67 StartY=3.12 StartZ=0 EndX=-34.67 EndY=6.42 EndZ=0
    g3: LineSegment [constr] StartX=-34.67 StartY=6.42 StartZ=0 EndX=-28.67 EndY=6.42 EndZ=0
    g4: LineSegment [constr] StartX=-28.67 StartY=6.42 StartZ=0 EndX=-28.67 EndY=3.12 EndZ=0
    g5: LineSegment [constr] StartX=-28.67 StartY=3.12 StartZ=0 EndX=-34.67 EndY=3.12 EndZ=0
    g6: GeomPoint [constr] X=-31.67 Y=4.77 Z=0
    g7: LineSegment [constr] StartX=-44.67 StartY=3.12 StartZ=0 EndX=-44.67 EndY=6.42 EndZ=0
    g8: LineSegment [constr] StartX=-44.67 StartY=6.42 StartZ=0 EndX=-38.67 EndY=6.42 EndZ=0
    g9: LineSegment [constr] StartX=-38.67 StartY=6.42 StartZ=0 EndX=-38.67 EndY=3.12 EndZ=0
    g10: LineSegment [constr] StartX=-38.67 StartY=3.12 StartZ=0 EndX=-44.67 EndY=3.12 EndZ=0
    g11: GeomPoint [constr] X=-41.67 Y=4.77 Z=0
    g12: LineSegment [constr] StartX=-24.67 StartY=3.12 StartZ=0 EndX=-24.67 EndY=6.42 EndZ=0
    g13: LineSegment [constr] StartX=-24.67 StartY=6.42 StartZ=0 EndX=-18.67 EndY=6.42 EndZ=0
    g14: LineSegment [constr] StartX=-18.67 StartY=6.42 StartZ=0 EndX=-18.67 EndY=3.12 EndZ=0
    g15: LineSegment [constr] StartX=-18.67 StartY=3.12 StartZ=0 EndX=-24.67 EndY=3.12 EndZ=0
    g16: GeomPoint [constr] X=-21.67 Y=4.77 Z=0
    g17: LineSegment [constr] StartX=-14.67 StartY=3.12 StartZ=0 EndX=-14.67 EndY=6.42 EndZ=0
    g18: LineSegment [constr] StartX=-14.67 StartY=6.42 StartZ=0 EndX=-8.67 EndY=6.42 EndZ=0
    g19: LineSegment [constr] StartX=-8.67 StartY=6.42 StartZ=0 EndX=-8.67 EndY=3.12 EndZ=0
    g20: LineSegment [constr] StartX=-8.67 StartY=3.12 StartZ=0 EndX=-14.67 EndY=3.12 EndZ=0
    g21: GeomPoint [constr] X=-11.67 Y=4.77 Z=0
    g22: ArcOfCircle CenterX=-30.17 CenterY=4.77 CenterZ=0 NormalX=0 NormalY=0 NormalZ=1 AngleXU=0 Radius=1.5 StartAngle=4.71239 EndAngle=7.85398
    g23: ArcOfCircle CenterX=-33.17 CenterY=4.77 CenterZ=0 NormalX=0 NormalY=0 NormalZ=1 AngleXU=0 Radius=1.5 StartAngle=1.5708 EndAngle=4.71239
    g24: LineSegment StartX=-30.17 StartY=6.27 StartZ=0 EndX=-33.17 EndY=6.27 EndZ=0
    g25: LineSegment StartX=-33.17 StartY=3.27 StartZ=0 EndX=-30.17 EndY=3.27 EndZ=0
    g26: ArcOfCircle CenterX=-23.17 CenterY=4.77 CenterZ=0 NormalX=0 NormalY=0 NormalZ=1 AngleXU=0 Radius=1.5 StartAngle=1.5708 EndAngle=4.71239
    g27: ArcOfCircle CenterX=-20.17 CenterY=4.77 CenterZ=0 NormalX=0 NormalY=0 NormalZ=1 AngleXU=0 Radius=1.5 StartAngle=4.71239 EndAngle=7.85398
    g28: LineSegment StartX=-23.17 StartY=3.27 StartZ=0 EndX=-20.17 EndY=3.27 EndZ=0
    g29: LineSegment StartX=-20.17 StartY=6.27 StartZ=0 EndX=-23.17 EndY=6.27 EndZ=0
    g30: ArcOfCircle CenterX=-13.17 CenterY=4.77 CenterZ=0 NormalX=0 NormalY=0 NormalZ=1 AngleXU=0 Radius=1.5 StartAngle=1.5708 EndAngle=4.71239
    g31: ArcOfCircle CenterX=-10.17 CenterY=4.77 CenterZ=0 NormalX=0 NormalY=0 NormalZ=1 AngleXU=0 Radius=1.5 StartAngle=4.71239 EndAngle=7.85398
    g32: LineSegment StartX=-13.17 StartY=3.27 StartZ=0 EndX=-10.17 EndY=3.27 EndZ=0
    g33: LineSegment StartX=-10.17 StartY=6.27 StartZ=0 EndX=-13.17 EndY=6.27 EndZ=0
    g34: ArcOfCircle CenterX=-40.17 CenterY=4.77 CenterZ=0 NormalX=0 NormalY=0 NormalZ=1 AngleXU=0 Radius=1.5 StartAngle=4.71239 EndAngle=7.85398
    g35: ArcOfCircle CenterX=-43.17 CenterY=4.77 CenterZ=0 NormalX=0 NormalY=0 NormalZ=1 AngleXU=0 Radius=1.5 StartAngle=1.5708 EndAngle=4.71239
    g36: LineSegment StartX=-40.17 StartY=6.27 StartZ=0 EndX=-43.17 EndY=6.27 EndZ=0
    g37: LineSegment StartX=-43.17 StartY=3.27 StartZ=0 EndX=-40.17 EndY=3.27 EndZ=0
    g38: GeomPoint [constr] X=-26.67 Y=11.37 Z=0
    g39: LineSegment [constr] StartX=6.27 StartY=4.77 StartZ=0 EndX=47.07 EndY=4.77 EndZ=0
    g40: ArcOfCircle CenterX=10.17 CenterY=4.77 CenterZ=0 NormalX=0 NormalY=0 NormalZ=1 AngleXU=0 Radius=1.5 StartAngle=1.5708 EndAngle=4.71239
    g41: ArcOfCircle CenterX=13.17 CenterY=4.77 CenterZ=0 NormalX=0 NormalY=0 NormalZ=1 AngleXU=0 Radius=1.5 StartAngle=4.71239 EndAngle=7.85398
    g42: LineSegment StartX=10.17 StartY=3.27 StartZ=0 EndX=13.17 EndY=3.27 EndZ=0
    g43: LineSegment StartX=13.17 StartY=6.27 StartZ=0 EndX=10.17 EndY=6.27 EndZ=0
    g44: ArcOfCircle CenterX=20.17 CenterY=4.77 CenterZ=0 NormalX=0 NormalY=0 NormalZ=1 AngleXU=0 Radius=1.5 StartAngle=1.5708 EndAngle=4.71239
    g45: ArcOfCircle CenterX=23.17 CenterY=4.77 CenterZ=0 NormalX=0 NormalY=0 NormalZ=1 AngleXU=0 Radius=1.5 StartAngle=4.71239 EndAngle=7.85398
    g46: LineSegment StartX=20.17 StartY=3.27 StartZ=0 EndX=23.17 EndY=3.27 EndZ=0
    g47: LineSegment StartX=23.17 StartY=6.27 StartZ=0 EndX=20.17 EndY=6.27 EndZ=0
    g48: ArcOfCircle CenterX=30.17 CenterY=4.77 CenterZ=0 NormalX=0 NormalY=0 NormalZ=1 AngleXU=0 Radius=1.5 StartAngle=1.5708 EndAngle=4.71239
    g49: ArcOfCircle CenterX=33.17 CenterY=4.77 CenterZ=0 NormalX=0 NormalY=0 NormalZ=1 AngleXU=0 Radius=1.5 StartAngle=4.71239 EndAngle=7.85398
    g50: LineSegment StartX=30.17 StartY=3.27 StartZ=0 EndX=33.17 EndY=3.27 EndZ=0
    g51: LineSegment StartX=33.17 StartY=6.27 StartZ=0 EndX=30.17 EndY=6.27 EndZ=0
    g52: ArcOfCircle CenterX=43.17 CenterY=4.77 CenterZ=0 NormalX=0 NormalY=0 NormalZ=1 AngleXU=0 Radius=1.5 StartAngle=4.71239 EndAngle=7.85398
    g53: ArcOfCircle CenterX=40.17 CenterY=4.77 CenterZ=0 NormalX=0 NormalY=0 NormalZ=1 AngleXU=0 Radius=1.5 StartAngle=1.5708 EndAngle=4.71239
    g54: LineSegment StartX=43.17 StartY=6.27 StartZ=0 EndX=40.17 EndY=6.27 EndZ=0
    g55: LineSegment StartX=40.17 StartY=3.27 StartZ=0 EndX=43.17 EndY=3.27 EndZ=0
    g56: GeomPoint [constr] X=26.67 Y=4.77 Z=0
    g57: GeomPoint [constr] X=11.67 Y=4.77 Z=0
    g58: GeomPoint [constr] X=21.67 Y=4.77 Z=0
    g59: GeomPoint [constr] X=31.67 Y=4.77 Z=0
    g60: GeomPoint [constr] X=41.67 Y=4.77 Z=0
    g61: LineSegment [constr] StartX=-33.32 StartY=2.695 StartZ=0 EndX=-30.02 EndY=2.695 EndZ=0
    g62: LineSegment [constr] StartX=-29.02 StartY=3.695 StartZ=0 EndX=-29.02 EndY=5.845 EndZ=0
    g63: LineSegment [constr] StartX=-30.02 StartY=6.845 StartZ=0 EndX=-33.32 EndY=6.845 EndZ=0
    g64: LineSegment [constr] StartX=-34.32 StartY=5.845 StartZ=0 EndX=-34.32 EndY=3.695 EndZ=0
    g65: GeomPoint [constr] X=-31.67 Y=4.77 Z=0
    g66: ArcOfCircle [constr] CenterX=-33.32 CenterY=5.845 CenterZ=0 NormalX=0 NormalY=0 NormalZ=1 AngleXU=0 Radius=1 StartAngle=1.5708 EndAngle=3.14159
    g67: GeomPoint [constr] X=-34.32 Y=6.845 Z=0
    g68: ArcOfCircle [constr] CenterX=-33.32 CenterY=3.695 CenterZ=0 NormalX=0 NormalY=0 NormalZ=1 AngleXU=0 Radius=1 StartAngle=3.14159 EndAngle=4.71239
    g69: GeomPoint [constr] X=-34.32 Y=2.695 Z=0
    g70: ArcOfCircle [constr] CenterX=-30.02 CenterY=3.695 CenterZ=0 NormalX=0 NormalY=0 NormalZ=1 AngleXU=0 Radius=1 StartAngle=4.71239 EndAngle=6.28319
    g71: GeomPoint [constr] X=-29.02 Y=2.695 Z=0
    g72: ArcOfCircle [constr] CenterX=-30.02 CenterY=5.845 CenterZ=0 NormalX=0 NormalY=0 NormalZ=1 AngleXU=0 Radius=1 StartAngle=0 EndAngle=1.5708
    g73: GeomPoint [constr] X=-29.02 Y=6.845 Z=0
    g74: LineSegment [constr] StartX=-13.32 StartY=2.695 StartZ=0 EndX=-10.02 EndY=2.695 EndZ=0
    g75: LineSegment [constr] StartX=-9.02 StartY=3.695 StartZ=0 EndX=-9.02 EndY=5.845 EndZ=0
    g76: LineSegment [constr] StartX=-10.02 StartY=6.845 StartZ=0 EndX=-13.32 EndY=6.845 EndZ=0
    g77: LineSegment [constr] StartX=-14.32 StartY=5.845 StartZ=0 EndX=-14.32 EndY=3.695 EndZ=0
    g78: GeomPoint [constr] X=-11.67 Y=4.77 Z=0
    g79: ArcOfCircle [constr] CenterX=-13.32 CenterY=5.845 CenterZ=0 NormalX=0 NormalY=0 NormalZ=1 AngleXU=0 Radius=1 StartAngle=1.5708 EndAngle=3.14159
    g80: GeomPoint [constr] X=-14.32 Y=6.845 Z=0
    g81: ArcOfCircle [constr] CenterX=-13.32 CenterY=3.695 CenterZ=0 NormalX=0 NormalY=0 NormalZ=1 AngleXU=0 Radius=1 StartAngle=3.14159 EndAngle=4.71239
    g82: GeomPoint [constr] X=-14.32 Y=2.695 Z=0
    g83: ArcOfCircle [constr] CenterX=-10.02 CenterY=3.695 CenterZ=0 NormalX=0 NormalY=0 NormalZ=1 AngleXU=0 Radius=1 StartAngle=4.71239 EndAngle=6.28319
    g84: GeomPoint [constr] X=-9.02 Y=2.695 Z=0
    g85: ArcOfCircle [constr] CenterX=-10.02 CenterY=5.845 CenterZ=0 NormalX=0 NormalY=0 NormalZ=1 AngleXU=0 Radius=1 StartAngle=4e-16 EndAngle=1.5708
    g86: GeomPoint [constr] X=-9.02 Y=6.845 Z=0
    g87: LineSegment [constr] StartX=-23.32 StartY=2.695 StartZ=0 EndX=-20.02 EndY=2.695 EndZ=0
    g88: LineSegment [constr] StartX=-19.02 StartY=3.695 StartZ=0 EndX=-19.02 EndY=5.845 EndZ=0
    g89: LineSegment [constr] StartX=-20.02 StartY=6.845 StartZ=0 EndX=-23.32 EndY=6.845 EndZ=0
    g90: LineSegment [constr] StartX=-24.32 StartY=5.845 StartZ=0 EndX=-24.32 EndY=3.695 EndZ=0
    g91: GeomPoint [constr] X=-21.67 Y=4.77 Z=0
    g92: ArcOfCircle [constr] CenterX=-23.32 CenterY=5.845 CenterZ=0 NormalX=0 NormalY=0 NormalZ=1 AngleXU=0 Radius=1 StartAngle=1.5708 EndAngle=3.14159
    g93: GeomPoint [constr] X=-24.32 Y=6.845 Z=0
    g94: ArcOfCircle [constr] CenterX=-23.32 CenterY=3.695 CenterZ=0 NormalX=0 NormalY=0 NormalZ=1 AngleXU=0 Radius=1 StartAngle=3.14159 EndAngle=4.71239
    g95: GeomPoint [constr] X=-24.32 Y=2.695 Z=0
    g96: ArcOfCircle [constr] CenterX=-20.02 CenterY=3.695 CenterZ=0 NormalX=0 NormalY=0 NormalZ=1 AngleXU=0 Radius=1 StartAngle=4.71239 EndAngle=6.28319
    g97: GeomPoint [constr] X=-19.02 Y=2.695 Z=0
    g98: ArcOfCircle [constr] CenterX=-20.02 CenterY=5.845 CenterZ=0 NormalX=0 NormalY=0 NormalZ=1 AngleXU=0 Radius=1 StartAngle=0 EndAngle=1.5708
    g99: GeomPoint [constr] X=-19.02 Y=6.845 Z=0
    g100: LineSegment [constr] StartX=10.02 StartY=2.695 StartZ=0 EndX=13.32 EndY=2.695 EndZ=0
    g101: LineSegment [constr] StartX=14.32 StartY=3.695 StartZ=0 EndX=14.32 EndY=5.845 EndZ=0
    g102: LineSegment [constr] StartX=13.32 StartY=6.845 StartZ=0 EndX=10.02 EndY=6.845 EndZ=0
    g103: LineSegment [constr] StartX=9.02 StartY=5.845 StartZ=0 EndX=9.02 EndY=3.695 EndZ=0
    g104: GeomPoint [constr] X=11.67 Y=4.77 Z=0
    g105: ArcOfCircle [constr] CenterX=10.02 CenterY=5.845 CenterZ=0 NormalX=0 NormalY=0 NormalZ=1 AngleXU=0 Radius=1 StartAngle=1.5708 EndAngle=3.14159
    g106: GeomPoint [constr] X=9.02 Y=6.845 Z=0
    g107: ArcOfCircle [constr] CenterX=10.02 CenterY=3.695 CenterZ=0 NormalX=0 NormalY=0 NormalZ=1 AngleXU=0 Radius=1 StartAngle=3.14159 EndAngle=4.71239
    g108: GeomPoint [constr] X=9.02 Y=2.695 Z=0
    g109: ArcOfCircle [constr] CenterX=13.32 CenterY=3.695 CenterZ=0 NormalX=0 NormalY=0 NormalZ=1 AngleXU=0 Radius=1 StartAngle=4.71239 EndAngle=6.28319
    g110: GeomPoint [constr] X=14.32 Y=2.695 Z=0
    g111: ArcOfCircle [constr] CenterX=13.32 CenterY=5.845 CenterZ=0 NormalX=0 NormalY=0 NormalZ=1 AngleXU=0 Radius=1 StartAngle=3e-16 EndAngle=1.5708
    g112: GeomPoint [constr] X=14.32 Y=6.845 Z=0
    g113: LineSegment [constr] StartX=20.02 StartY=2.695 StartZ=0 EndX=23.32 EndY=2.695 EndZ=0
    g114: LineSegment [constr] StartX=24.32 StartY=3.695 StartZ=0 EndX=24.32 EndY=5.845 EndZ=0
    g115: LineSegment [constr] StartX=23.32 StartY=6.845 StartZ=0 EndX=20.02 EndY=6.845 EndZ=0
    g116: LineSegment [constr] StartX=19.02 StartY=5.845 StartZ=0 EndX=19.02 EndY=3.695 EndZ=0
    g117: GeomPoint [constr] X=21.67 Y=4.77 Z=0
    g118: ArcOfCircle [constr] CenterX=20.02 CenterY=5.845 CenterZ=0 NormalX=0 NormalY=0 NormalZ=1 AngleXU=0 Radius=1 StartAngle=1.5708 EndAngle=3.14159
    g119: GeomPoint [constr] X=19.02 Y=6.845 Z=0
    g120: ArcOfCircle [constr] CenterX=20.02 CenterY=3.695 CenterZ=0 NormalX=0 NormalY=0 NormalZ=1 AngleXU=0 Radius=1 StartAngle=3.14159 EndAngle=4.71239
    g121: GeomPoint [constr] X=19.02 Y=2.695 Z=0
    g122: ArcOfCircle [constr] CenterX=23.32 CenterY=3.695 CenterZ=0 NormalX=0 NormalY=0 NormalZ=1 AngleXU=0 Radius=1 StartAngle=4.71239 EndAngle=6.28319
    g123: GeomPoint [constr] X=24.32 Y=2.695 Z=0
    g124: ArcOfCircle [constr] CenterX=23.32 CenterY=5.845 CenterZ=0 NormalX=0 NormalY=0 NormalZ=1 AngleXU=0 Radius=1 StartAngle=0 EndAngle=1.5708
    g125: GeomPoint [constr] X=24.32 Y=6.845 Z=0
    g126: LineSegment [constr] StartX=30.02 StartY=2.695 StartZ=0 EndX=33.32 EndY=2.695 EndZ=0
    g127: LineSegment [constr] StartX=34.32 StartY=3.695 StartZ=0 EndX=34.32 EndY=5.845 EndZ=0
    g128: LineSegment [constr] StartX=33.32 StartY=6.845 StartZ=0 EndX=30.02 EndY=6.845 EndZ=0
    g129: LineSegment [constr] StartX=29.02 StartY=5.845 StartZ=0 EndX=29.02 EndY=3.695 EndZ=0
    g130: GeomPoint [constr] X=31.67 Y=4.77 Z=0
    g131: ArcOfCircle [constr] CenterX=30.02 CenterY=5.845 CenterZ=0 NormalX=0 NormalY=0 NormalZ=1 AngleXU=0 Radius=1 StartAngle=1.5708 EndAngle=3.14159
    g132: GeomPoint [constr] X=29.02 Y=6.845 Z=0
    g133: ArcOfCircle [constr] CenterX=30.02 CenterY=3.695 CenterZ=0 NormalX=0 NormalY=0 NormalZ=1 AngleXU=0 Radius=1 StartAngle=3.14159 EndAngle=4.71239
    g134: GeomPoint [constr] X=29.02 Y=2.695 Z=0
    g135: ArcOfCircle [constr] CenterX=33.32 CenterY=3.695 CenterZ=0 NormalX=0 NormalY=0 NormalZ=1 AngleXU=0 Radius=1 StartAngle=4.71239 EndAngle=6.28319
    g136: GeomPoint [constr] X=34.32 Y=2.695 Z=0
    g137: ArcOfCircle [constr] CenterX=33.32 CenterY=5.845 CenterZ=0 NormalX=0 NormalY=0 NormalZ=1 AngleXU=0 Radius=1 StartAngle=1e-16 EndAngle=1.5708
    g138: GeomPoint [constr] X=34.32 Y=6.845 Z=0
    g139: LineSegment [constr] StartX=40.02 StartY=2.695 StartZ=0 EndX=43.32 EndY=2.695 EndZ=0
    g140: LineSegment [constr] StartX=44.32 StartY=3.695 StartZ=0 EndX=44.32 EndY=5.845 EndZ=0
    g141: LineSegment [constr] StartX=43.32 StartY=6.845 StartZ=0 EndX=40.02 EndY=6.845 EndZ=0
    g142: LineSegment [constr] StartX=39.02 StartY=5.845 StartZ=0 EndX=39.02 EndY=3.695 EndZ=0
    g143: GeomPoint [constr] X=41.67 Y=4.77 Z=0
    g144: ArcOfCircle [constr] CenterX=40.02 CenterY=5.845 CenterZ=0 NormalX=0 NormalY=0 NormalZ=1 AngleXU=0 Radius=1 StartAngle=1.5708 EndAngle=3.14159
    g145: GeomPoint [constr] X=39.02 Y=6.845 Z=0
    g146: ArcOfCircle [constr] CenterX=40.02 CenterY=3.695 CenterZ=0 NormalX=0 NormalY=0 NormalZ=1 AngleXU=0 Radius=1 StartAngle=3.14159 EndAngle=4.71239
    g147: GeomPoint [constr] X=39.02 Y=2.695 Z=0
    g148: ArcOfCircle [constr] CenterX=43.32 CenterY=3.695 CenterZ=0 NormalX=0 NormalY=0 NormalZ=1 AngleXU=0 Radius=1 StartAngle=4.71239 EndAngle=6.28319
    g149: GeomPoint [constr] X=44.32 Y=2.695 Z=0
    g150: ArcOfCircle [constr] CenterX=43.32 CenterY=5.845 CenterZ=0 NormalX=0 NormalY=0 NormalZ=1 AngleXU=0 Radius=1 StartAngle=1e-16 EndAngle=1.5708
    g151: GeomPoint [constr] X=44.32 Y=6.845 Z=0
    g152: LineSegment [constr] StartX=-43.32 StartY=2.695 StartZ=0 EndX=-40.02 EndY=2.695 EndZ=0
    g153: LineSegment [constr] StartX=-39.02 StartY=3.695 StartZ=0 EndX=-39.02 EndY=5.845 EndZ=0
    g154: LineSegment [constr] StartX=-40.02 StartY=6.845 StartZ=0 EndX=-43.32 EndY=6.845 EndZ=0
    g155: LineSegment [constr] StartX=-44.32 StartY=5.845 StartZ=0 EndX=-44.32 EndY=3.695 EndZ=0
    g156: GeomPoint [constr] X=-41.67 Y=4.77 Z=0
    g157: ArcOfCircle [constr] CenterX=-43.32 CenterY=5.845 CenterZ=0 NormalX=0 NormalY=0 NormalZ=1 AngleXU=0 Radius=1 StartAngle=1.5708 EndAngle=3.14159
    g158: GeomPoint [constr] X=-44.32 Y=6.845 Z=0
    g159: ArcOfCircle [constr] CenterX=-43.32 CenterY=3.695 CenterZ=0 NormalX=0 NormalY=0 NormalZ=1 AngleXU=0 Radius=1 StartAngle=3.14159 EndAngle=4.71239
    g160: GeomPoint [constr] X=-44.32 Y=2.695 Z=0
    g161: ArcOfCircle [constr] CenterX=-40.02 CenterY=3.695 CenterZ=0 NormalX=0 NormalY=0 NormalZ=1 AngleXU=0 Radius=1 StartAngle=4.71239 EndAngle=6.28319
    g162: GeomPoint [constr] X=-39.02 Y=2.695 Z=0
    g163: ArcOfCircle [constr] CenterX=-40.02 CenterY=5.845 CenterZ=0 NormalX=0 NormalY=0 NormalZ=1 AngleXU=0 Radius=1 StartAngle=1e-16 EndAngle=1.5708
    g164: GeomPoint [constr] X=-39.02 Y=6.845 Z=0
    g165: ArcOfCircle [constr] CenterX=-42.67 CenterY=4.77 CenterZ=0 NormalX=0 NormalY=0 NormalZ=1 AngleXU=0 Radius=0.9 StartAngle=1.5708 EndAngle=4.71239
    g166: ArcOfCircle [constr] CenterX=-40.67 CenterY=4.77 CenterZ=0 NormalX=0 NormalY=0 NormalZ=1 AngleXU=0 Radius=0.9 StartAngle=4.71239 EndAngle=7.85398
    g167: LineSegment [constr] StartX=-42.67 StartY=5.67 StartZ=0 EndX=-40.67 EndY=5.67 EndZ=0
    g168: LineSegment [constr] StartX=-42.67 StartY=3.87 StartZ=0 EndX=-40.67 EndY=3.87 EndZ=0
    g169: ArcOfCircle [constr] CenterX=-32.67 CenterY=4.77 CenterZ=0 NormalX=0 NormalY=0 NormalZ=1 AngleXU=0 Radius=0.9 StartAngle=1.5708 EndAngle=4.71239
    g170: ArcOfCircle [constr] CenterX=-30.67 CenterY=4.77 CenterZ=0 NormalX=0 NormalY=0 NormalZ=1 AngleXU=0 Radius=0.9 StartAngle=4.71239 EndAngle=7.85398
    g171: LineSegment [constr] StartX=-32.67 StartY=5.67 StartZ=0 EndX=-30.67 EndY=5.67 EndZ=0
    g172: LineSegment [constr] StartX=-32.67 StartY=3.87 StartZ=0 EndX=-30.67 EndY=3.87 EndZ=0
    g173: ArcOfCircle [constr] CenterX=-22.67 CenterY=4.77 CenterZ=0 NormalX=0 NormalY=0 NormalZ=1 AngleXU=0 Radius=0.9 StartAngle=1.5708 EndAngle=4.71239
    g174: ArcOfCircle [constr] CenterX=-20.67 CenterY=4.77 CenterZ=0 NormalX=0 NormalY=0 NormalZ=1 AngleXU=0 Radius=0.9 StartAngle=4.71239 EndAngle=7.85398
    g175: LineSegment [constr] StartX=-22.67 StartY=5.67 StartZ=0 EndX=-20.67 EndY=5.67 EndZ=0
    g176: LineSegment [constr] StartX=-22.67 StartY=3.87 StartZ=0 EndX=-20.67 EndY=3.87 EndZ=0
    g177: ArcOfCircle [constr] CenterX=-12.67 CenterY=4.77 CenterZ=0 NormalX=0 NormalY=0 NormalZ=1 AngleXU=0 Radius=0.9 StartAngle=1.5708 EndAngle=4.71239
    g178: ArcOfCircle [constr] CenterX=-10.67 CenterY=4.77 CenterZ=0 NormalX=0 NormalY=0 NormalZ=1 AngleXU=0 Radius=0.9 StartAngle=4.71239 EndAngle=7.85398
    g179: LineSegment [constr] StartX=-12.67 StartY=5.67 StartZ=0 EndX=-10.67 EndY=5.67 EndZ=0
    g180: LineSegment [constr] StartX=-12.67 StartY=3.87 StartZ=0 EndX=-10.67 EndY=3.87 EndZ=0
    g181: ArcOfCircle [constr] CenterX=10.67 CenterY=4.77 CenterZ=0 NormalX=0 NormalY=0 NormalZ=1 AngleXU=0 Radius=0.9 StartAngle=1.5708 EndAngle=4.71239
    g182: ArcOfCircle [constr] CenterX=12.67 CenterY=4.77 CenterZ=0 NormalX=0 NormalY=0 NormalZ=1 AngleXU=0 Radius=0.9 StartAngle=4.71239 EndAngle=7.85398
    g183: LineSegment [constr] StartX=10.67 StartY=5.67 StartZ=0 EndX=12.67 EndY=5.67 EndZ=0
    g184: LineSegment [constr] StartX=10.67 StartY=3.87 StartZ=0 EndX=12.67 EndY=3.87 EndZ=0
    g185: ArcOfCircle [constr] CenterX=20.67 CenterY=4.77 CenterZ=0 NormalX=0 NormalY=0 NormalZ=1 AngleXU=0 Radius=0.9 StartAngle=1.5708 EndAngle=4.71239
    g186: ArcOfCircle [constr] CenterX=22.67 CenterY=4.77 CenterZ=0 NormalX=0 NormalY=0 NormalZ=1 AngleXU=0 Radius=0.9 StartAngle=4.71239 EndAngle=7.85398
    g187: LineSegment [constr] StartX=20.67 StartY=5.67 StartZ=0 EndX=22.67 EndY=5.67 EndZ=0
    g188: LineSegment [constr] StartX=20.67 StartY=3.87 StartZ=0 EndX=22.67 EndY=3.87 EndZ=0
    g189: ArcOfCircle [constr] CenterX=32.67 CenterY=4.77 CenterZ=0 NormalX=0 NormalY=0 NormalZ=1 AngleXU=0 Radius=0.9 StartAngle=4.71239 EndAngle=7.85398
    g190: ArcOfCircle [constr] CenterX=30.67 CenterY=4.77 CenterZ=0 NormalX=0 NormalY=0 NormalZ=1 AngleXU=0 Radius=0.9 StartAngle=1.5708 EndAngle=4.71239
    g191: LineSegment [constr] StartX=32.67 StartY=3.87 StartZ=0 EndX=30.67 EndY=3.87 EndZ=0
    g192: LineSegment [constr] StartX=32.67 StartY=5.67 StartZ=0 EndX=30.67 EndY=5.67 EndZ=0
    g193: ArcOfCircle [constr] CenterX=40.67 CenterY=4.77 CenterZ=0 NormalX=0 NormalY=0 NormalZ=1 AngleXU=0 Radius=0.9 StartAngle=1.5708 EndAngle=4.71239
    g194: ArcOfCircle [constr] CenterX=42.67 CenterY=4.77 CenterZ=0 NormalX=0 NormalY=0 NormalZ=1 AngleXU=0 Radius=0.9 StartAngle=4.71239 EndAngle=7.85398
    g195: LineSegment [constr] StartX=40.67 StartY=5.67 StartZ=0 EndX=42.67 EndY=5.67 EndZ=0
    g196: LineSegment [constr] StartX=40.67 StartY=3.87 StartZ=0 EndX=42.67 EndY=3.87 EndZ=0
    g197: Circle [constr] CenterX=-41.67 CenterY=4.77 CenterZ=0 NormalX=0 NormalY=0 NormalZ=1 AngleXU=0 Radius=1.5
    g198: Circle [constr] CenterX=-31.67 CenterY=4.77 CenterZ=0 NormalX=0 NormalY=0 NormalZ=1 AngleXU=0 Radius=1.5
    g199: Circle [constr] CenterX=-21.67 CenterY=4.77 CenterZ=0 NormalX=0 NormalY=0 NormalZ=1 AngleXU=0 Radius=1.5
    g200: Circle [constr] CenterX=-11.67 CenterY=4.77 CenterZ=0 NormalX=0 NormalY=0 NormalZ=1 AngleXU=0 Radius=1.5
    g201: Circle [constr] CenterX=11.67 CenterY=4.77 CenterZ=0 NormalX=0 NormalY=0 NormalZ=1 AngleXU=0 Radius=1.5
    g202: Circle [constr] CenterX=21.67 CenterY=4.77 CenterZ=0 NormalX=0 NormalY=0 NormalZ=1 AngleXU=0 Radius=1.5
    g203: Circle [constr] CenterX=31.67 CenterY=4.77 CenterZ=0 NormalX=0 NormalY=0 NormalZ=1 AngleXU=0 Radius=1.5
    g204: Circle [constr] CenterX=41.67 CenterY=4.77 CenterZ=0 NormalX=0 NormalY=0 NormalZ=1 AngleXU=0 Radius=1.5
  constraints (452):
    c: Horizontal(g0)
    c: DistanceX(g0,g0) = 40.8
    c: Symmetric(g0,g0,g1)
    c: DistanceX(g1,g-1) = 26.67
    c: Coincident(g2,g3)
    c: Coincident(g3,g4)
    c: Coincident(g4,g5)
    c: Coincident(g5,g2)
    c: Horizontal(g3)
    c: Horizontal(g5)
    c: Vertical(g2)
    c: Vertical(g4)
    c: Symmetric(g3,g2,g6)
    c: PointOnObject(g6,g0)
    c: Coincident(g7,g8)
    c: Coincident(g8,g9)
    c: Coincident(g9,g10)
    c: Coincident(g10,g7)
    c: Horizontal(g8)
    c: Horizontal(g10)
    c: Vertical(g7)
    c: Vertical(g9)
    c: Symmetric(g8,g7,g11)
    c: PointOnObject(g11,g0)
    c: Coincident(g12,g13)
    c: Coincident(g13,g14)
    c: Coincident(g14,g15)
    c: Coincident(g15,g12)
    c: Horizontal(g13)
    c: Horizontal(g15)
    c: Vertical(g12)
    c: Vertical(g14)
    c: Symmetric(g13,g12,g16)
    c: Coincident(g17,g18)
    c: Coincident(g18,g19)
    c: Coincident(g19,g20)
    c: Coincident(g20,g17)
    c: Horizontal(g18)
    c: Horizontal(g20)
    c: Vertical(g17)
    c: Vertical(g19)
    c: Symmetric(g18,g17,g21)
    c: Symmetric(g16,g6,g1)
    c: Symmetric(g11,g21,g1)
    c: Equal(g13,g3)
    c: Equal(g3,g8)
    c: Equal(g8,g18)
    c: Equal(g14,g17)
    c: Equal(g17,g4)
    c: Equal(g4,g9)
    c: DistanceX(g13,g13) = 6
    c: DistanceY(g19,g19) = 3.3
    c: Tangent(g22,g24) = -1.5708
    c: Tangent(g24,g23) = -1.5708
    c: Tangent(g23,g25) = -1.5708
    c: Tangent(g25,g22) = -1.5708
    c: Equal(g22,g23)
    c: PointOnObject(g22,g0)
    c: Tangent(g26,g28) = -1.5708
    c: Tangent(g28,g27) = -1.5708
    c: Tangent(g27,g29) = -1.5708
    c: Tangent(g29,g26) = -1.5708
    c: Equal(g26,g27)
    c: PointOnObject(g26,g0)
    c: Tangent(g30,g32) = -1.5708
    c: Tangent(g32,g31) = -1.5708
    c: Tangent(g31,g33) = -1.5708
    c: Tangent(g33,g30) = -1.5708
    c: Equal(g30,g31)
    c: PointOnObject(g30,g0)
    c: Tangent(g34,g36) = -1.5708
    c: Tangent(g36,g35) = -1.5708
    c: Tangent(g35,g37) = -1.5708
    c: Tangent(g37,g34) = -1.5708
    c: Equal(g34,g35)
    c: PointOnObject(g34,g0)
    c: Equal(g35,g23)
    c: Equal(g23,g27)
    c: Equal(g27,g31)
    c: Equal(g29,g33)
    c: Equal(g33,g25)
    c: Equal(g25,g37)
    c: Symmetric(g34,g35,g11)
    c: Symmetric(g22,g23,g6)
    c: Symmetric(g26,g27,g16)
    c: Symmetric(g30,g31,g21)
    c: Diameter(g31) = 3
    c: DistanceX(g33,g33) = 3
    c: DistanceY(g-1,g38) = 11.37
    c: Vertical(g38,g1)
    c: DistanceY(g23,g38) = 8.1
    c: DistanceY(g-1,g0) = 4.77
    c: Horizontal(g39)
    c: Tangent(g40,g42) = -1.5708
    c: Tangent(g42,g41) = -1.5708
    c: Tangent(g41,g43) = -1.5708
    c: Tangent(g43,g40) = -1.5708
    c: Equal(g40,g41)
    c: PointOnObject(g40,g39)
    c: PointOnObject(g41,g39)
    c: Tangent(g44,g46) = -1.5708
    c: Tangent(g46,g45) = -1.5708
    c: Tangent(g45,g47) = -1.5708
    c: Tangent(g47,g44) = -1.5708
    c: Equal(g44,g45)
    c: PointOnObject(g44,g39)
    c: PointOnObject(g45,g39)
    c: Tangent(g48,g50) = -1.5708
    c: Tangent(g50,g49) = -1.5708
    c: Tangent(g49,g51) = -1.5708
    c: Tangent(g51,g48) = -1.5708
    c: Equal(g48,g49)
    c: PointOnObject(g48,g39)
    c: Tangent(g52,g54) = -1.5708
    c: Tangent(g54,g53) = -1.5708
    c: Tangent(g53,g55) = -1.5708
    c: Tangent(g55,g52) = -1.5708
    c: Equal(g52,g53)
    c: PointOnObject(g52,g39)
    c: Equal(g31,g40)
    c: Equal(g40,g44)
    c: Equal(g44,g48)
    c: Equal(g48,g52)
    c: Symmetric(g39,g0,g-2)
    c: Equal(g33,g43)
    c: Equal(g43,g47)
    c: Equal(g47,g51)
    c: Equal(g51,g55)
    c: DistanceX(g6,g16) = 10
    c: DistanceX(g16,g21) = 10
    c: Equal(g0,g39)
    c: Symmetric(g39,g39,g56)
    c: Symmetric(g52,g53,g60)
    c: Symmetric(g49,g48,g59)
    c: Symmetric(g44,g45,g58)
    c: Symmetric(g41,g40,g57)
    c: Symmetric(g58,g59,g56)
    c: DistanceX(g58,g59) = 10
    c: DistanceX(g57,g58) = 10
    c: Symmetric(g57,g60,g56)
    c: Horizontal(g61)
    c: Horizontal(g63)
    c: Vertical(g62)
    c: Vertical(g64)
    c: Symmetric(g73,g69,g65)
    c: PointOnObject(g67,g63)
    c: PointOnObject(g67,g64)
    c: Tangent(g63,g66) = -1.5708
    c: Tangent(g64,g66) = -1.5708
    c: PointOnObject(g69,g64)
    c: PointOnObject(g69,g61)
    c: Tangent(g64,g68) = -1.5708
    c: Tangent(g61,g68) = -1.5708
    c: PointOnObject(g71,g62)
    c: PointOnObject(g71,g61)
    c: Tangent(g62,g70) = -1.5708
    c: Tangent(g61,g70) = -1.5708
    c: PointOnObject(g73,g62)
    c: PointOnObject(g73,g63)
    c: Tangent(g62,g72) = -1.5708
    c: Tangent(g63,g72) = -1.5708
    c: Equal(g68,g70)
    c: Equal(g70,g72)
    c: Equal(g72,g66)
    c: Horizontal(g74)
    c: Horizontal(g76)
    c: Vertical(g75)
    c: Vertical(g77)
    c: Symmetric(g86,g82,g78)
    c: PointOnObject(g80,g76)
    c: PointOnObject(g80,g77)
    c: Tangent(g76,g79) = -1.5708
    c: Tangent(g77,g79) = -1.5708
    c: PointOnObject(g82,g77)
    c: PointOnObject(g82,g74)
    c: Tangent(g77,g81) = -1.5708
    c: Tangent(g74,g81) = -1.5708
    c: PointOnObject(g84,g75)
    c: PointOnObject(g84,g74)
    c: Tangent(g75,g83) = -1.5708
    c: Tangent(g74,g83) = -1.5708
    c: PointOnObject(g86,g75)
    c: PointOnObject(g86,g76)
    c: Tangent(g75,g85) = -1.5708
    c: Tangent(g76,g85) = -1.5708
    c: Equal(g81,g83)
    c: Equal(g83,g85)
    c: Equal(g85,g79)
    c: Horizontal(g87)
    c: Horizontal(g89)
    c: Vertical(g88)
    c: Vertical(g90)
    c: Symmetric(g99,g95,g91)
    c: PointOnObject(g93,g89)
    c: PointOnObject(g93,g90)
    c: Tangent(g89,g92) = -1.5708
    c: Tangent(g90,g92) = -1.5708
    c: PointOnObject(g95,g90)
    c: PointOnObject(g95,g87)
    c: Tangent(g90,g94) = -1.5708
    c: Tangent(g87,g94) = -1.5708
    c: PointOnObject(g97,g88)
    c: PointOnObject(g97,g87)
    c: Tangent(g88,g96) = -1.5708
    c: Tangent(g87,g96) = -1.5708
    c: PointOnObject(g99,g88)
    c: PointOnObject(g99,g89)
    c: Tangent(g88,g98) = -1.5708
    c: Tangent(g89,g98) = -1.5708
    c: Equal(g94,g96)
    c: Equal(g96,g98)
    c: Equal(g98,g92)
    c: Horizontal(g100)
    c: Horizontal(g102)
    c: Vertical(g101)
    c: Vertical(g103)
    c: Symmetric(g112,g108,g104)
    c: PointOnObject(g106,g102)
    c: PointOnObject(g106,g103)
    c: Tangent(g102,g105) = -1.5708
    c: Tangent(g103,g105) = -1.5708
    c: PointOnObject(g108,g103)
    c: PointOnObject(g108,g100)
    c: Tangent(g103,g107) = -1.5708
    c: Tangent(g100,g107) = -1.5708
    c: PointOnObject(g110,g101)
    c: PointOnObject(g110,g100)
    c: Tangent(g101,g109) = -1.5708
    c: Tangent(g100,g109) = -1.5708
    c: PointOnObject(g112,g101)
    c: PointOnObject(g112,g102)
    c: Tangent(g101,g111) = -1.5708
    c: Tangent(g102,g111) = -1.5708
    c: Equal(g107,g109)
    c: Equal(g109,g111)
    c: Equal(g111,g105)
    c: Horizontal(g113)
    c: Horizontal(g115)
    c: Vertical(g114)
    c: Vertical(g116)
    c: Symmetric(g125,g121,g117)
    c: PointOnObject(g119,g115)
    c: PointOnObject(g119,g116)
    c: Tangent(g115,g118) = -1.5708
    c: Tangent(g116,g118) = -1.5708
    c: PointOnObject(g121,g116)
    c: PointOnObject(g121,g113)
    c: Tangent(g116,g120) = -1.5708
    c: Tangent(g113,g120) = -1.5708
    c: PointOnObject(g123,g114)
    c: PointOnObject(g123,g113)
    c: Tangent(g114,g122) = -1.5708
    c: Tangent(g113,g122) = -1.5708
    c: PointOnObject(g125,g114)
    c: PointOnObject(g125,g115)
    c: Tangent(g114,g124) = -1.5708
    c: Tangent(g115,g124) = -1.5708
    c: Equal(g120,g122)
    c: Equal(g122,g124)
    c: Equal(g124,g118)
    c: Horizontal(g126)
    c: Horizontal(g128)
    c: Vertical(g127)
    c: Vertical(g129)
    c: Symmetric(g138,g134,g130)
    c: PointOnObject(g132,g128)
    c: PointOnObject(g132,g129)
    c: Tangent(g128,g131) = -1.5708
    c: Tangent(g129,g131) = -1.5708
    c: PointOnObject(g134,g129)
    c: PointOnObject(g134,g126)
    c: Tangent(g129,g133) = -1.5708
    c: Tangent(g126,g133) = -1.5708
    c: PointOnObject(g136,g127)
    c: PointOnObject(g136,g126)
    c: Tangent(g127,g135) = -1.5708
    c: Tangent(g126,g135) = -1.5708
    c: PointOnObject(g138,g127)
    c: PointOnObject(g138,g128)
    c: Tangent(g127,g137) = -1.5708
    c: Tangent(g128,g137) = -1.5708
    c: Equal(g133,g135)
    c: Equal(g135,g137)
    c: Equal(g137,g131)
    c: Horizontal(g139)
    c: Horizontal(g141)
    c: Vertical(g140)
    c: Vertical(g142)
    c: Symmetric(g151,g147,g143)
    c: PointOnObject(g145,g141)
    c: PointOnObject(g145,g142)
    c: Tangent(g141,g144) = -1.5708
    c: Tangent(g142,g144) = -1.5708
    c: PointOnObject(g147,g142)
    c: PointOnObject(g147,g139)
    c: Tangent(g142,g146) = -1.5708
    c: Tangent(g139,g146) = -1.5708
    c: PointOnObject(g149,g140)
    c: PointOnObject(g149,g139)
    c: Tangent(g140,g148) = -1.5708
    c: Tangent(g139,g148) = -1.5708
    c: PointOnObject(g151,g140)
    c: PointOnObject(g151,g141)
    c: Tangent(g140,g150) = -1.5708
    c: Tangent(g141,g150) = -1.5708
    c: Equal(g146,g148)
    c: Equal(g148,g150)
    c: Equal(g150,g144)
    c: Horizontal(g152)
    c: Horizontal(g154)
    c: Vertical(g153)
    c: Vertical(g155)
    c: Symmetric(g164,g160,g156)
    c: PointOnObject(g158,g154)
    c: PointOnObject(g158,g155)
    c: Tangent(g154,g157) = -1.5708
    c: Tangent(g155,g157) = -1.5708
    c: PointOnObject(g160,g155)
    c: PointOnObject(g160,g152)
    c: Tangent(g155,g159) = -1.5708
    c: Tangent(g152,g159) = -1.5708
    c: PointOnObject(g162,g153)
    c: PointOnObject(g162,g152)
    c: Tangent(g153,g161) = -1.5708
    c: Tangent(g152,g161) = -1.5708
    c: PointOnObject(g164,g153)
    c: PointOnObject(g164,g154)
    c: Tangent(g153,g163) = -1.5708
    c: Tangent(g154,g163) = -1.5708
    c: Equal(g159,g161)
    c: Equal(g161,g163)
    c: Equal(g163,g157)
    c: DistanceY(g152,g154) = 4.15
    c: Diameter(g157) = 2
    c: DistanceX(g155,g153) = 5.3
    c: Equal(g154,g63)
    c: Equal(g63,g89)
    c: Equal(g89,g76)
    c: Equal(g76,g128)
    c: Equal(g128,g115)
    c: Equal(g115,g102)
    c: Equal(g102,g141)
    c: Equal(g155,g64)
    c: Equal(g64,g90)
    c: Equal(g90,g77)
    c: Equal(g77,g142)
    c: Equal(g142,g129)
    c: Equal(g129,g116)
    c: Equal(g116,g103)
    c: Equal(g66,g92)
    c: Equal(g92,g79)
    c: Equal(g79,g144)
    c: Equal(g144,g131)
    c: Equal(g131,g118)
    c: Equal(g118,g105)
    c: Equal(g105,g157)
    c: Coincident(g156,g11)
    c: Coincident(g65,g6)
    c: Coincident(g91,g16)
    c: Coincident(g78,g21)
    c: Coincident(g104,g57)
    c: Coincident(g117,g58)
    c: Coincident(g130,g59)
    c: Coincident(g143,g60)
    c: Tangent(g165,g167) = 1.5708
    c: Tangent(g165,g168) = -1.5708
    c: Tangent(g166,g167) = 1.5708
    c: Tangent(g166,g168) = -1.5708
    c: Equal(g165,g166)
    c: Horizontal(g168)
    c: Tangent(g169,g171) = 1.5708
    c: Tangent(g169,g172) = -1.5708
    c: Tangent(g170,g171) = 1.5708
    c: Tangent(g170,g172) = -1.5708
    c: Equal(g169,g170)
    c: Horizontal(g172)
    c: Tangent(g173,g175) = 1.5708
    c: Tangent(g173,g176) = -1.5708
    c: Tangent(g174,g175) = 1.5708
    c: Tangent(g174,g176) = -1.5708
    c: Equal(g173,g174)
    c: Horizontal(g176)
    c: Tangent(g177,g179) = 1.5708
    c: Tangent(g177,g180) = -1.5708
    c: Tangent(g178,g179) = 1.5708
    c: Tangent(g178,g180) = -1.5708
    c: Equal(g177,g178)
    c: Horizontal(g180)
    c: Tangent(g181,g183) = 1.5708
    c: Tangent(g181,g184) = -1.5708
    c: Tangent(g182,g183) = 1.5708
    c: Tangent(g182,g184) = -1.5708
    c: Equal(g181,g182)
    c: Horizontal(g184)
    c: Tangent(g185,g187) = 1.5708
    c: Tangent(g185,g188) = -1.5708
    c: Tangent(g186,g187) = 1.5708
    c: Tangent(g186,g188) = -1.5708
    c: Equal(g185,g186)
    c: Horizontal(g188)
    c: Tangent(g189,g191) = 1.5708
    c: Tangent(g189,g192) = -1.5708
    c: Tangent(g190,g191) = 1.5708
    c: Tangent(g190,g192) = -1.5708
    c: Equal(g189,g190)
    c: Horizontal(g192)
    c: Tangent(g193,g195) = 1.5708
    c: Tangent(g193,g196) = -1.5708
    c: Tangent(g194,g195) = 1.5708
    c: Tangent(g194,g196) = -1.5708
    c: Equal(g193,g194)
    c: Horizontal(g196)
    c: Equal(g165,g169)
    c: Equal(g169,g173)
    c: Equal(g173,g177)
    c: Equal(g177,g181)
    c: Equal(g181,g185)
    c: Equal(g185,g190)
    c: Equal(g190,g193)
    c: Symmetric(g165,g166,g11)
    c: Symmetric(g169,g170,g6)
    c: Symmetric(g174,g173,g16)
    c: Symmetric(g177,g178,g21)
    c: Symmetric(g181,g182,g57)
    c: Symmetric(g185,g186,g58)
    c: Symmetric(g190,g189,g59)
    c: Symmetric(g193,g194,g60)
    c: Diameter(g165) = 1.8
    c: DistanceX(g167,g167) = 2
    c: Equal(g167,g171)
    c: Equal(g171,g175)
    c: Equal(g175,g179)
    c: Equal(g179,g183)
    c: Equal(g183,g187)
    c: Equal(g187,g192)
    c: Equal(g192,g195)
    c: Coincident(g197,g11)
    c: Coincident(g198,g6)
    c: Coincident(g199,g16)
    c: Coincident(g200,g21)
    c: Coincident(g201,g57)
    c: Coincident(g202,g58)
    c: Coincident(g203,g59)
    c: Coincident(g204,g60)
    c: Equal(g197,g198)
    c: Equal(g198,g199)
    c: Equal(g199,g200)
    c: Equal(g200,g201)
    c: Equal(g201,g202)
    c: Equal(g202,g203)
    c: Equal(g203,g204)
    c: Diameter(g197) = 3
FEATURE [PartDesign::Pocket] Pocket010  label="TEK1_button"
  BaseFeature = -> Pocket008
  Direction = (0,0,-1)
  Length = 5
  Length2 = 5
  Profile = -> Sketch029
  ReferenceAxis = -> Sketch029 [N_Axis]
  Suppressed = false
  Type = 0
FEATURE [TechDraw::DrawSVGTemplate] Template002
  Height = 210
  Orientation = 1
  Template = C:/Program Files/FreeCAD 0.21/data/Mod/TechDraw/Templates/A4_Landscape_blank.svg
  Width = 297
FEATURE [TechDraw::DrawViewAnnotation] Annotation002
  Font = osifont
  LineSpace = 100
  LockPosition = false
  MaxWidth = -1
  Rotation = 0
  ScaleType = 0
  Text = The mid of the datum plane A is preferred to be near | to the lower limit of the flatness tolerance zone. | It can be achieved with an additional bending step. | Aesthetical surfaces colored red on the view | No scratches, burrs or any kind of damage allowed! | Functional surfaces colored blue on the view (all which perpendicular to the aesthetical) | No burrs or other protruding material allowed!
  TextSize = 3
  TextStyle = 0
  X = 97.2718
  Y = 52.2376
FEATURE [TechDraw::DrawViewAnnotation] Annotation003
  Font = osifont
  LineSpace = 100
  LockPosition = false
  MaxWidth = -1
  Rotation = 0
  ScaleType = 0
  Text = The mid of the datum plane A is preferred to be near | to the lower limit of the flatness tolerance zone. | It can be achieved with an additional bending step.
  TextSize = 4
  TextStyle = 0
  X = 283.844
  Y = 84.5906
FEATURE [Sketcher::SketchObject] Sketch030  label="TEK2_ButtonHole001"
  ArcFitTolerance = 0
  AttachmentSupport = -> [XY_Plane011]
  FullyConstrained = true
  MakeInternals = false
  MapMode = 5
  sketch-geometry (97):
    g0: Circle [constr] CenterX=-40.005 CenterY=-13.335 CenterZ=0 NormalX=0 NormalY=0 NormalZ=1 AngleXU=0 Radius=2
    g1: Circle [constr] CenterX=-13.335 CenterY=-13.335 CenterZ=0 NormalX=0 NormalY=0 NormalZ=1 AngleXU=0 Radius=2
    g2: LineSegment [constr] StartX=-40.005 StartY=-13.335 StartZ=0 EndX=-13.335 EndY=-13.335 EndZ=0
    g3: Circle [constr] CenterX=13.335 CenterY=-13.335 CenterZ=0 NormalX=0 NormalY=0 NormalZ=1 AngleXU=0 Radius=2
    g4: LineSegment [constr] StartX=-13.335 StartY=-13.335 StartZ=0 EndX=13.335 EndY=-13.335 EndZ=0
    g5: Circle [constr] CenterX=40.005 CenterY=-13.335 CenterZ=0 NormalX=0 NormalY=0 NormalZ=1 AngleXU=0 Radius=2
    g6: LineSegment [constr] StartX=13.335 StartY=-13.335 StartZ=0 EndX=40.005 EndY=-13.335 EndZ=0
    g7: Circle [constr] CenterX=-40.005 CenterY=-40.005 CenterZ=0 NormalX=0 NormalY=0 NormalZ=1 AngleXU=0 Radius=2
    g8: LineSegment [constr] StartX=-40.005 StartY=-13.335 StartZ=0 EndX=-40.005 EndY=-40.005 EndZ=0
    g9: Circle [constr] CenterX=-13.335 CenterY=-40.005 CenterZ=0 NormalX=0 NormalY=0 NormalZ=1 AngleXU=0 Radius=2
    g10: LineSegment [constr] StartX=-40.005 StartY=-40.005 StartZ=0 EndX=-13.335 EndY=-40.005 EndZ=0
    g11: Circle [constr] CenterX=13.335 CenterY=-40.005 CenterZ=0 NormalX=0 NormalY=0 NormalZ=1 AngleXU=0 Radius=2
    g12: LineSegment [constr] StartX=-13.335 StartY=-40.005 StartZ=0 EndX=13.335 EndY=-40.005 EndZ=0
    g13: Circle [constr] CenterX=40.005 CenterY=-40.005 CenterZ=0 NormalX=0 NormalY=0 NormalZ=1 AngleXU=0 Radius=2
    g14: LineSegment [constr] StartX=13.335 StartY=-40.005 StartZ=0 EndX=40.005 EndY=-40.005 EndZ=0
    g15: LineSegment [constr] StartX=0 StartY=0 StartZ=0 EndX=13.335 EndY=-13.335 EndZ=0
    g16: LineSegment [constr] StartX=0 StartY=0 StartZ=0 EndX=-13.335 EndY=-13.335 EndZ=0
    g17: LineSegment StartX=-48.505 StartY=-19.735 StartZ=0 EndX=-48.505 EndY=-6.935 EndZ=0
    g18: LineSegment StartX=-46.405 StartY=-4.835 StartZ=0 EndX=-33.605 EndY=-4.835 EndZ=0
    g19: LineSegment StartX=-31.505 StartY=-6.935 StartZ=0 EndX=-31.505 EndY=-19.735 EndZ=0
    g20: LineSegment StartX=-33.605 StartY=-21.835 StartZ=0 EndX=-46.405 EndY=-21.835 EndZ=0
    g21: GeomPoint [constr] X=-40.005 Y=-13.335 Z=0
    g22: LineSegment StartX=-21.835 StartY=-19.735 StartZ=0 EndX=-21.835 EndY=-6.935 EndZ=0
    g23: LineSegment StartX=-19.735 StartY=-4.835 StartZ=0 EndX=-6.935 EndY=-4.835 EndZ=0
    g24: LineSegment StartX=-4.835 StartY=-6.935 StartZ=0 EndX=-4.835 EndY=-19.735 EndZ=0
    g25: LineSegment StartX=-6.935 StartY=-21.835 StartZ=0 EndX=-19.735 EndY=-21.835 EndZ=0
    g26: GeomPoint [constr] X=-13.335 Y=-13.335 Z=0
    g27: LineSegment StartX=4.835 StartY=-19.735 StartZ=0 EndX=4.835 EndY=-6.935 EndZ=0
    g28: LineSegment StartX=6.935 StartY=-4.835 StartZ=0 EndX=19.735 EndY=-4.835 EndZ=0
    g29: LineSegment StartX=21.835 StartY=-6.935 StartZ=0 EndX=21.835 EndY=-19.735 EndZ=0
    g30: LineSegment StartX=19.735 StartY=-21.835 StartZ=0 EndX=6.935 EndY=-21.835 EndZ=0
    g31: GeomPoint [constr] X=13.335 Y=-13.335 Z=0
    g32: LineSegment StartX=31.505 StartY=-19.735 StartZ=0 EndX=31.505 EndY=-6.935 EndZ=0
    g33: LineSegment StartX=33.605 StartY=-4.835 StartZ=0 EndX=46.405 EndY=-4.835 EndZ=0
    g34: LineSegment StartX=48.505 StartY=-6.935 StartZ=0 EndX=48.505 EndY=-19.735 EndZ=0
    g35: LineSegment StartX=46.405 StartY=-21.835 StartZ=0 EndX=33.605 EndY=-21.835 EndZ=0
    g36: GeomPoint [constr] X=40.005 Y=-13.335 Z=0
    g37: LineSegment StartX=31.505 StartY=-46.405 StartZ=0 EndX=31.505 EndY=-33.605 EndZ=0
    g38: LineSegment StartX=33.605 StartY=-31.505 StartZ=0 EndX=46.405 EndY=-31.505 EndZ=0
    g39: LineSegment StartX=48.505 StartY=-33.605 StartZ=0 EndX=48.505 EndY=-46.405 EndZ=0
    g40: LineSegment StartX=46.405 StartY=-48.505 StartZ=0 EndX=33.605 EndY=-48.505 EndZ=0
    g41: GeomPoint [constr] X=40.005 Y=-40.005 Z=0
    g42: LineSegment StartX=4.835 StartY=-46.405 StartZ=0 EndX=4.835 EndY=-33.605 EndZ=0
    g43: LineSegment StartX=6.935 StartY=-31.505 StartZ=0 EndX=19.735 EndY=-31.505 EndZ=0
    g44: LineSegment StartX=21.835 StartY=-33.605 StartZ=0 EndX=21.835 EndY=-46.405 EndZ=0
    g45: LineSegment StartX=19.735 StartY=-48.505 StartZ=0 EndX=6.935 EndY=-48.505 EndZ=0
    g46: GeomPoint [constr] X=13.335 Y=-40.005 Z=0
    g47: LineSegment StartX=-21.835 StartY=-46.405 StartZ=0 EndX=-21.835 EndY=-33.605 EndZ=0
    g48: LineSegment StartX=-19.735 StartY=-31.505 StartZ=0 EndX=-6.935 EndY=-31.505 EndZ=0
    g49: LineSegment StartX=-4.835 StartY=-33.605 StartZ=0 EndX=-4.835 EndY=-46.405 EndZ=0
    g50: LineSegment StartX=-6.935 StartY=-48.505 StartZ=0 EndX=-19.735 EndY=-48.505 EndZ=0
    g51: GeomPoint [constr] X=-13.335 Y=-40.005 Z=0
    g52: LineSegment StartX=-48.505 StartY=-46.405 StartZ=0 EndX=-48.505 EndY=-33.605 EndZ=0
    g53: LineSegment StartX=-46.405 StartY=-31.505 StartZ=0 EndX=-33.605 EndY=-31.505 EndZ=0
    g54: LineSegment StartX=-31.505 StartY=-33.605 StartZ=0 EndX=-31.505 EndY=-46.405 EndZ=0
    g55: LineSegment StartX=-33.605 StartY=-48.505 StartZ=0 EndX=-46.405 EndY=-48.505 EndZ=0
    g56: GeomPoint [constr] X=-40.005 Y=-40.005 Z=0
    g57: ArcOfCircle CenterX=-46.405 CenterY=-6.935 CenterZ=0 NormalX=0 NormalY=0 NormalZ=1 AngleXU=0 Radius=2.1 StartAngle=1.5708 EndAngle=3.14159
    g58: ArcOfCircle CenterX=-33.605 CenterY=-6.935 CenterZ=0 NormalX=0 NormalY=0 NormalZ=1 AngleXU=0 Radius=2.1 StartAngle=0 EndAngle=1.5708
    g59: ArcOfCircle CenterX=-33.605 CenterY=-19.735 CenterZ=0 NormalX=0 NormalY=0 NormalZ=1 AngleXU=0 Radius=2.1 StartAngle=4.71239 EndAngle=6.28319
    g60: ArcOfCircle CenterX=-46.405 CenterY=-19.735 CenterZ=0 NormalX=0 NormalY=0 NormalZ=1 AngleXU=0 Radius=2.1 StartAngle=3.14159 EndAngle=4.71239
    g61: ArcOfCircle CenterX=-19.735 CenterY=-6.935 CenterZ=0 NormalX=0 NormalY=0 NormalZ=1 AngleXU=0 Radius=2.1 StartAngle=1.5708 EndAngle=3.14159
    g62: ArcOfCircle CenterX=-19.735 CenterY=-19.735 CenterZ=0 NormalX=0 NormalY=0 NormalZ=1 AngleXU=0 Radius=2.1 StartAngle=3.14159 EndAngle=4.71239
    g63: ArcOfCircle CenterX=-6.935 CenterY=-19.735 CenterZ=0 NormalX=0 NormalY=0 NormalZ=1 AngleXU=0 Radius=2.1 StartAngle=4.71239 EndAngle=6.28319
    g64: ArcOfCircle CenterX=-6.935 CenterY=-6.935 CenterZ=0 NormalX=0 NormalY=0 NormalZ=1 AngleXU=0 Radius=2.1 StartAngle=0 EndAngle=1.5708
    g65: ArcOfCircle CenterX=6.935 CenterY=-6.935 CenterZ=0 NormalX=0 NormalY=0 NormalZ=1 AngleXU=0 Radius=2.1 StartAngle=1.5708 EndAngle=3.14159
    g66: ArcOfCircle CenterX=19.735 CenterY=-6.935 CenterZ=0 NormalX=0 NormalY=0 NormalZ=1 AngleXU=0 Radius=2.1 StartAngle=0 EndAngle=1.5708
    g67: ArcOfCircle CenterX=19.735 CenterY=-19.735 CenterZ=0 NormalX=0 NormalY=0 NormalZ=1 AngleXU=0 Radius=2.1 StartAngle=4.71239 EndAngle=6.28319
    g68: ArcOfCircle CenterX=6.935 CenterY=-19.735 CenterZ=0 NormalX=0 NormalY=0 NormalZ=1 AngleXU=0 Radius=2.1 StartAngle=3.14159 EndAngle=4.71239
    g69: ArcOfCircle CenterX=33.605 CenterY=-19.735 CenterZ=0 NormalX=0 NormalY=0 NormalZ=1 AngleXU=0 Radius=2.1 StartAngle=3.14159 EndAngle=4.71239
    g70: ArcOfCircle CenterX=46.405 CenterY=-6.935 CenterZ=0 NormalX=0 NormalY=0 NormalZ=1 AngleXU=0 Radius=2.1 StartAngle=0 EndAngle=1.5708
    g71: ArcOfCircle CenterX=33.605 CenterY=-6.935 CenterZ=0 NormalX=0 NormalY=0 NormalZ=1 AngleXU=0 Radius=2.1 StartAngle=1.5708 EndAngle=3.14159
    g72: ArcOfCircle CenterX=46.405 CenterY=-19.735 CenterZ=0 NormalX=0 NormalY=0 NormalZ=1 AngleXU=0 Radius=2.1 StartAngle=4.71239 EndAngle=6.28319
    g73: ArcOfCircle CenterX=33.605 CenterY=-33.605 CenterZ=0 NormalX=0 NormalY=0 NormalZ=1 AngleXU=0 Radius=2.1 StartAngle=1.5708 EndAngle=3.14159
    g74: ArcOfCircle CenterX=46.405 CenterY=-46.405 CenterZ=0 NormalX=0 NormalY=0 NormalZ=1 AngleXU=0 Radius=2.1 StartAngle=4.71239 EndAngle=6.28319
    g75: ArcOfCircle CenterX=46.405 CenterY=-33.605 CenterZ=0 NormalX=0 NormalY=0 NormalZ=1 AngleXU=0 Radius=2.1 StartAngle=-9e-16 EndAngle=1.5708
    g76: ArcOfCircle CenterX=33.605 CenterY=-46.405 CenterZ=0 NormalX=0 NormalY=0 NormalZ=1 AngleXU=0 Radius=2.1 StartAngle=3.14159 EndAngle=4.71239
    g77: ArcOfCircle CenterX=6.935 CenterY=-33.605 CenterZ=0 NormalX=0 NormalY=0 NormalZ=1 AngleXU=0 Radius=2.1 StartAngle=1.5708 EndAngle=3.14159
    g78: ArcOfCircle CenterX=19.735 CenterY=-33.605 CenterZ=0 NormalX=0 NormalY=0 NormalZ=1 AngleXU=0 Radius=2.1 StartAngle=-9e-16 EndAngle=1.5708
    g79: ArcOfCircle CenterX=19.735 CenterY=-46.405 CenterZ=0 NormalX=0 NormalY=0 NormalZ=1 AngleXU=0 Radius=2.1 StartAngle=4.71239 EndAngle=6.28319
    g80: ArcOfCircle CenterX=6.935 CenterY=-46.405 CenterZ=0 NormalX=0 NormalY=0 NormalZ=1 AngleXU=0 Radius=2.1 StartAngle=3.14159 EndAngle=4.71239
    g81: ArcOfCircle CenterX=-6.935 CenterY=-33.605 CenterZ=0 NormalX=0 NormalY=0 NormalZ=1 AngleXU=0 Radius=2.1 StartAngle=-1.8e-15 EndAngle=1.5708
    g82: ArcOfCircle CenterX=-19.735 CenterY=-46.405 CenterZ=0 NormalX=0 NormalY=0 NormalZ=1 AngleXU=0 Radius=2.1 StartAngle=3.14159 EndAngle=4.71239
    g83: ArcOfCircle CenterX=-19.735 CenterY=-33.605 CenterZ=0 NormalX=0 NormalY=0 NormalZ=1 AngleXU=0 Radius=2.1 StartAngle=1.5708 EndAngle=3.14159
    g84: ArcOfCircle CenterX=-6.935 CenterY=-46.405 CenterZ=0 NormalX=0 NormalY=0 NormalZ=1 AngleXU=0 Radius=2.1 StartAngle=4.71239 EndAngle=6.28319
    g85: ArcOfCircle CenterX=-46.405 CenterY=-33.605 CenterZ=0 NormalX=0 NormalY=0 NormalZ=1 AngleXU=0 Radius=2.1 StartAngle=1.5708 EndAngle=3.14159
    g86: ArcOfCircle CenterX=-33.605 CenterY=-33.605 CenterZ=0 NormalX=0 NormalY=0 NormalZ=1 AngleXU=0 Radius=2.1 StartAngle=-1.8e-15 EndAngle=1.5708
    g87: ArcOfCircle CenterX=-46.405 CenterY=-46.405 CenterZ=0 NormalX=0 NormalY=0 NormalZ=1 AngleXU=0 Radius=2.1 StartAngle=3.14159 EndAngle=4.71239
    g88: ArcOfCircle CenterX=-33.605 CenterY=-46.405 CenterZ=0 NormalX=0 NormalY=0 NormalZ=1 AngleXU=0 Radius=2.1 StartAngle=4.71239 EndAngle=6.28319
    g89: LineSegment [constr] StartX=-40.005 StartY=-4.835 StartZ=0 EndX=-40.005 EndY=-21.835 EndZ=0
    g90: LineSegment [constr] StartX=-13.335 StartY=-4.835 StartZ=0 EndX=-13.335 EndY=-21.835 EndZ=0
    g91: LineSegment [constr] StartX=13.335 StartY=-4.835 StartZ=0 EndX=13.335 EndY=-21.835 EndZ=0
    g92: LineSegment [constr] StartX=40.005 StartY=-4.835 StartZ=0 EndX=40.005 EndY=-21.835 EndZ=0
    g93: LineSegment [constr] StartX=40.005 StartY=-31.505 StartZ=0 EndX=40.005 EndY=-48.505 EndZ=0
    g94: LineSegment [constr] StartX=13.335 StartY=-31.505 StartZ=0 EndX=13.335 EndY=-48.505 EndZ=0
    g95: LineSegment [constr] StartX=-13.335 StartY=-31.505 StartZ=0 EndX=-13.335 EndY=-48.505 EndZ=0
    g96: LineSegment [constr] StartX=-40.005 StartY=-31.505 StartZ=0 EndX=-40.005 EndY=-48.505 EndZ=0
  constraints (226):
    c: Diameter(g0) = 4
    c: Coincident(g0,g2)
    c: Coincident(g1,g2)
    c: Coincident(g1,g4)
    c: Coincident(g3,g4)
    c: Coincident(g3,g6)
    c: Coincident(g5,g6)
    c: Coincident(g0,g8)
    c: Coincident(g7,g8)
    c: Coincident(g7,g10)
    c: Coincident(g9,g10)
    c: Coincident(g9,g12)
    c: Coincident(g11,g12)
    c: Coincident(g11,g14)
    c: Coincident(g13,g14)
    c: Coincident(g-1,g16)
    c: Coincident(g16,g1)
    c: Coincident(g15,g3)
    c: Horizontal(g4)
    c: Horizontal(g2)
    c: Horizontal(g6)
    c: Horizontal(g10)
    c: Horizontal(g12)
    c: Horizontal(g14)
    c: Vertical(g8)
    c: Equal(g8,g2)
    c: Equal(g2,g10)
    c: Equal(g10,g12)
    c: Equal(g12,g4)
    c: Equal(g4,g6)
    c: Equal(g6,g14)
    c: DistanceX(g4,g4) = 26.67
    c: Equal(g16,g15)
    c: Coincident(g15,g16)
    c: Perpendicular(g15,g16)
    c: Equal(g7,g9)
    c: Equal(g9,g11)
    c: Equal(g11,g13)
    c: Equal(g13,g5)
    c: Equal(g5,g3)
    c: Equal(g3,g1)
    c: Equal(g1,g0)
    c: Horizontal(g18)
    c: Horizontal(g20)
    c: Vertical(g17)
    c: Vertical(g19)
    c: Coincident(g21,g0)
    c: Horizontal(g23)
    c: Horizontal(g25)
    c: Vertical(g22)
    c: Vertical(g24)
    c: Coincident(g26,g1)
    c: Horizontal(g28)
    c: Horizontal(g30)
    c: Vertical(g27)
    c: Vertical(g29)
    c: Coincident(g31,g3)
    c: Horizontal(g33)
    c: Horizontal(g35)
    c: Vertical(g32)
    c: Vertical(g34)
    c: Coincident(g36,g5)
    c: Horizontal(g38)
    c: Horizontal(g40)
    c: Vertical(g37)
    c: Vertical(g39)
    c: Coincident(g41,g13)
    c: Horizontal(g43)
    c: Horizontal(g45)
    c: Vertical(g42)
    c: Vertical(g44)
    c: Coincident(g46,g11)
    c: Horizontal(g48)
    c: Horizontal(g50)
    c: Vertical(g47)
    c: Vertical(g49)
    c: Coincident(g51,g9)
    c: Horizontal(g53)
    c: Horizontal(g55)
    c: Vertical(g52)
    c: Vertical(g54)
    c: Coincident(g56,g7)
    c: Tangent(g18,g57) = 1.5708
    c: Tangent(g17,g57) = 1.5708
    c: Tangent(g18,g58) = 1.5708
    c: Tangent(g19,g58) = 1.5708
    c: Tangent(g19,g59) = 1.5708
    c: Tangent(g20,g59) = 1.5708
    c: Tangent(g20,g60) = 1.5708
    c: Tangent(g17,g60) = 1.5708
    c: Tangent(g23,g61) = 1.5708
    c: Tangent(g22,g61) = 1.5708
    c: Tangent(g22,g62) = 1.5708
    c: Tangent(g25,g62) = 1.5708
    c: Tangent(g24,g63) = 1.5708
    c: Tangent(g25,g63) = 1.5708
    c: Tangent(g23,g64) = 1.5708
    c: Tangent(g24,g64) = 1.5708
    c: Tangent(g27,g65) = 1.5708
    c: Tangent(g28,g65) = 1.5708
    c: Tangent(g28,g66) = 1.5708
    c: Tangent(g29,g66) = 1.5708
    c: Tangent(g29,g67) = 1.5708
    c: Tangent(g30,g67) = 1.5708
    c: Tangent(g27,g68) = 1.5708
    c: Tangent(g30,g68) = 1.5708
    c: Tangent(g32,g69) = 1.5708
    c: Tangent(g35,g69) = 1.5708
    c: Tangent(g33,g70) = 1.5708
    c: Tangent(g34,g70) = 1.5708
    c: Tangent(g33,g71) = 1.5708
    c: Tangent(g32,g71) = 1.5708
    c: Tangent(g34,g72) = 1.5708
    c: Tangent(g35,g72) = 1.5708
    c: Tangent(g38,g73) = 1.5708
    c: Tangent(g37,g73) = 1.5708
    c: Tangent(g39,g74) = 1.5708
    c: Tangent(g40,g74) = 1.5708
    c: Tangent(g38,g75) = 1.5708
    c: Tangent(g39,g75) = 1.5708
    c: Tangent(g37,g76) = 1.5708
    c: Tangent(g40,g76) = 1.5708
    c: Tangent(g43,g77) = 1.5708
    c: Tangent(g42,g77) = 1.5708
    c: Tangent(g43,g78) = 1.5708
    c: Tangent(g44,g78) = 1.5708
    c: Tangent(g44,g79) = 1.5708
    c: Tangent(g45,g79) = 1.5708
    c: Tangent(g42,g80) = 1.5708
    c: Tangent(g45,g80) = 1.5708
    c: Tangent(g48,g81) = 1.5708
    c: Tangent(g49,g81) = 1.5708
    c: Tangent(g47,g82) = 1.5708
    c: Tangent(g50,g82) = 1.5708
    c: Tangent(g47,g83) = 1.5708
    c: Tangent(g48,g83) = 1.5708
    c: Tangent(g49,g84) = 1.5708
    c: Tangent(g50,g84) = 1.5708
    c: Tangent(g53,g85) = 1.5708
    c: Tangent(g52,g85) = 1.5708
    c: Tangent(g53,g86) = 1.5708
    c: Tangent(g54,g86) = 1.5708
    c: Tangent(g55,g87) = 1.5708
    c: Tangent(g52,g87) = 1.5708
    c: Tangent(g54,g88) = 1.5708
    c: Tangent(g55,g88) = 1.5708
    c: Equal(g57,g58)
    c: Equal(g58,g59)
    c: Equal(g59,g60)
    c: Equal(g60,g85)
    c: Equal(g85,g86)
    c: Equal(g86,g88)
    c: Equal(g88,g87)
    c: Equal(g87,g61)
    c: Equal(g61,g64)
    c: Equal(g64,g63)
    c: Equal(g63,g62)
    c: Equal(g62,g68)
    c: Equal(g68,g67)
    c: Equal(g67,g65)
    c: Equal(g65,g66)
    c: Equal(g66,g71)
    c: Equal(g71,g70)
    c: Equal(g70,g72)
    c: Equal(g72,g69)
    c: Equal(g69,g73)
    c: Equal(g73,g75)
    c: Equal(g75,g74)
    c: Equal(g74,g76)
    c: Equal(g76,g78)
    c: Equal(g78,g77)
    c: Equal(g77,g80)
    c: Equal(g80,g79)
    c: Equal(g79,g81)
    c: Equal(g81,g83)
    c: Equal(g83,g82)
    c: Equal(g82,g84)
    c: Equal(g20,g19)
    c: Diameter(g57) = 4.2
    c: Equal(g40,g39)
    c: Equal(g39,g45)
    c: Equal(g45,g44)
    c: Equal(g44,g50)
    c: Equal(g50,g49)
    c: Equal(g49,g55)
    c: Equal(g55,g54)
    c: PointOnObject(g89,g20)
    c: Vertical(g89)
    c: DistanceY(g20,g18) = 17
    c: Symmetric(g18,g18,g89)
    c: PointOnObject(g90,g25)
    c: Vertical(g90)
    c: PointOnObject(g91,g30)
    c: Vertical(g91)
    c: PointOnObject(g92,g35)
    c: PointOnObject(g93,g40)
    c: PointOnObject(g94,g45)
    c: Vertical(g94)
    c: PointOnObject(g95,g50)
    c: PointOnObject(g96,g55)
    c: Vertical(g96)
    c: Symmetric(g23,g23,g90)
    c: Symmetric(g28,g28,g91)
    c: Vertical(g92)
    c: Symmetric(g33,g33,g92)
    c: Vertical(g93)
    c: Symmetric(g38,g38,g93)
    c: Symmetric(g43,g43,g94)
    c: Vertical(g95)
    c: Symmetric(g48,g48,g95)
    c: Symmetric(g53,g53,g96)
    c: Equal(g20,g25)
    c: Equal(g25,g24)
    c: Equal(g24,g30)
    c: Equal(g30,g29)
    c: Equal(g29,g35)
    c: Equal(g35,g34)
    c: Equal(g34,g55)
    c: Symmetric(g96,g96,g7)
    c: Symmetric(g95,g95,g9)
    c: Symmetric(g94,g94,g11)
    c: Symmetric(g93,g93,g13)
    c: Symmetric(g92,g92,g5)
    c: Symmetric(g91,g91,g3)
    c: Symmetric(g90,g90,g1)
    c: Symmetric(g89,g89,g0)
FEATURE [PartDesign::Pocket] Pocket011  label="TEK2_ButtonHole002"
  BaseFeature = -> Pocket010
  Direction = (0,0,-1)
  Length = 5
  Length2 = 5
  Profile = -> Sketch030
  ReferenceAxis = -> Sketch030 [N_Axis]
  Suppressed = false
  Type = 1
FEATURE [PartDesign::Body] Body011  label="FRONTPANEL-SHEET-VSN2"
  AllowCompound = false
  BaseFeature = -> Body
  Group = -> [Clone009,Sketch023,Sketch024,Sketch025,Sketch026,Sketch027,Pocket008,Sketch028,Sketch029,Pocket010,Sketch030,Pocket011]
  Origin = -> Origin011
  Tip = -> Pocket011
FEATURE [TechDraw::DrawViewPart] View
  CoarseView = false
  Direction = (0,0,1)
  Focus = 100
  HardHidden = true
  IsoCount = 0
  IsoHidden = false
  IsoVisible = false
  LockPosition = false
  Perspective = false
  Rotation = 0
  ScaleType = 0
  ScrubCount = 0
  SeamHidden = false
  SeamVisible = true
  SmoothHidden = false
  SmoothVisible = true
  Source = -> [Body011]
  X = 123.684
  XDirection = (1,0,0)
  Y = 197.398
FEATURE [TechDraw::DrawViewPart] View001
  CoarseView = false
  Direction = (-1,0,0)
  Focus = 100
  HardHidden = true
  IsoCount = 0
  IsoHidden = false
  IsoVisible = false
  LockPosition = false
  Perspective = false
  Rotation = 0
  ScaleType = 0
  ScrubCount = 0
  SeamHidden = false
  SeamVisible = true
  SmoothHidden = false
  SmoothVisible = true
  Source = -> [Body011]
  X = 217.392
  XDirection = (0,0,1)
  Y = 197.186
FEATURE [TechDraw::DrawViewPart] View002
  CoarseView = false
  Direction = (0,0,-1)
  Focus = 100
  HardHidden = true
  IsoCount = 0
  IsoHidden = false
  IsoVisible = false
  LockPosition = false
  Perspective = false
  Rotation = 0
  ScaleType = 0
  ScrubCount = 0
  SeamHidden = false
  SeamVisible = true
  SmoothHidden = false
  SmoothVisible = true
  Source = -> [Body011]
  X = 309.133
  XDirection = (-1,0,0)
  Y = 197.302
FEATURE [TechDraw::DrawViewDimension] Dimension
  AngleOverride = false
  Arbitrary = false
  ArbitraryTolerances = false
  EqualTolerance = false
  ExtensionAngle = 0
  FormatSpec = %.2w
  FormatSpecOverTolerance = %+.2w
  FormatSpecUnderTolerance = %+.2w
  Inverted = false
  LineAngle = 0
  LockPosition = false
  MeasureType = 1
  OverTolerance = 0
  References2D = -> [View]
  Rotation = 0
  ScaleType = 0
  TheoreticalExact = false
  Type = 2
  UnderTolerance = -0.2
  X = 61.7953
  Y = 1.34438
FEATURE [TechDraw::DrawViewBalloon] Balloon
  BubbleShape = 6
  EndType = 6
  EndTypeScale = 1
  KinkLength = 0
  LockPosition = false
  OriginX = 70.4982
  OriginY = 52.3109
  Rotation = 0
  ScaleType = 0
  ShapeScale = 1
  SourceView = -> Dimension
  Text = C
  TextWrapLen = -1
  X = 70.6756
  Y = 62.9547
FEATURE [TechDraw::DrawViewBalloon] Balloon002
  BubbleShape = 6
  EndType = 0
  EndTypeScale = 1
  KinkLength = -0.1
  LockPosition = false
  OriginX = 0.5
  OriginY = 0
  Rotation = 0
  ScaleType = 0
  ShapeScale = 1
  SourceView = -> View001
  Text = ⏥|0.2
  TextWrapLen = -1
  X = 19.0698
  Y = 0.107397
FEATURE [TechDraw::DrawViewBalloon] Balloon003
  BubbleShape = 6
  EndType = 6
  EndTypeScale = 1
  KinkLength = -0.1
  LockPosition = false
  OriginX = 0.672888
  OriginY = 39.7383
  Rotation = 0
  ScaleType = 0
  ShapeScale = 1
  SourceView = -> View001
  Text = A
  TextWrapLen = -1
  X = 10.7916
  Y = 39.8457
FEATURE [TechDraw::DrawViewBalloon] Balloon008
  BubbleShape = 1
  EndType = 0
  EndTypeScale = 1
  KinkLength = -0.1
  LockPosition = false
  OriginX = -52.0652
  OriginY = 52.0652
  Rotation = 0
  ScaleType = 0
  ShapeScale = 1
  SourceView = -> View
  Text = 4× R0.38
  TextWrapLen = -1
  X = -75.4388
  Y = 68.3556
FEATURE [TechDraw::DrawComplexSection] ComplexSection  label="Section A - A"
  BaseView = -> View
  Caption = Section A-A
  CoarseView = false
  CutSurfaceDisplay = 2
  CuttingToolWireObject = -> Sketch026
  Direction = (1e-16,-1,0)
  FileGeomPattern = C:/Program Files/FreeCAD 0.21/data/Mod/TechDraw/PAT/FCPAT.pat
  FileHatchPattern = C:/Program Files/FreeCAD 0.21/data/Mod/TechDraw/Patterns/simple.svg
  Focus = 100
  FuseBeforeCut = false
  HardHidden = true
  HatchOffset = (0,0,0)
  HatchRotation = 0
  HatchScale = 1
  IsoCount = 0
  IsoHidden = false
  IsoVisible = false
  LockPosition = false
  NameGeomPattern = Gyémánt bevonatú
  Perspective = false
  ProjectionStrategy = 1
  Rotation = 0
  Scale = 10
  ScaleType = 2
  ScrubCount = 0
  SeamHidden = false
  SeamVisible = true
  SectionDirection = 4
  SectionLineStretch = 1
  SectionNormal = (1e-16,-1,0)
  SectionOrigin = (0,0,0)
  SectionSymbol = A
  SmoothHidden = false
  SmoothVisible = true
  Source = -> [Body011]
  TrimAfterCut = false
  UsePreviousCut = false
  X = 287.429
  XDirection = (1,1e-16,0)
  Y = 98.2237
FEATURE [TechDraw::DrawViewDimension] Dimension008
  AngleOverride = false
  Arbitrary = false
  ArbitraryTolerances = false
  EqualTolerance = true
  ExtensionAngle = 0
  FormatSpec = 4x ⌀%.2w
  FormatSpecOverTolerance = %+.2w
  FormatSpecUnderTolerance = %+.2w
  Inverted = false
  LineAngle = 0
  LockPosition = false
  MeasureType = 1
  OverTolerance = 0
  References2D = -> [ComplexSection]
  Rotation = 0
  ScaleType = 0
  TheoreticalExact = false
  Type = 1
  UnderTolerance = 0
  X = 25.5096
  Y = 18.3127
FEATURE [TechDraw::DrawViewDimension] Dimension009
  AngleOverride = false
  Arbitrary = false
  ArbitraryTolerances = false
  EqualTolerance = true
  ExtensionAngle = 0
  FormatSpec = 4x ⌀%.2w
  FormatSpecOverTolerance = %+.2w
  FormatSpecUnderTolerance = %+.2w
  Inverted = false
  LineAngle = 0
  LockPosition = false
  MeasureType = 1
  OverTolerance = 0.05
  References2D = -> [ComplexSection]
  Rotation = 0
  ScaleType = 0
  TheoreticalExact = false
  Type = 1
  UnderTolerance = -0.05
  X = 48.7908
  Y = -4.80347
FEATURE [TechDraw::DrawViewBalloon] Balloon012
  BubbleShape = 6
  EndType = 6
  EndTypeScale = 1
  KinkLength = 0
  LockPosition = false
  OriginX = 46.1954
  OriginY = -17.0078
  Rotation = 0
  ScaleType = 0
  ShapeScale = 1
  SourceView = -> Dimension009
  Text = ⌖|⌀ 0.15|A|B|C
  TextWrapLen = -1
  X = 60.6339
  Y = -15.8915
FEATURE [TechDraw::DrawViewDimension] Dimension010
  AngleOverride = false
  Arbitrary = false
  ArbitraryTolerances = false
  EqualTolerance = true
  ExtensionAngle = 0
  FormatSpec = (%.2w)
  FormatSpecOverTolerance = %+.2w
  FormatSpecUnderTolerance = %+.2w
  Inverted = false
  LineAngle = 0
  LockPosition = false
  MeasureType = 1
  OverTolerance = 0
  References2D = -> [ComplexSection]
  Rotation = 0
  ScaleType = 0
  TheoreticalExact = false
  Type = 2
  UnderTolerance = 0
  X = -36.693
  Y = 2
FEATURE [TechDraw::DrawViewPart] View003
  CoarseView = false
  Direction = (0.57735,0.57735,0.57735)
  Focus = 100
  HardHidden = true
  IsoCount = 0
  IsoHidden = false
  IsoVisible = false
  LockPosition = false
  Perspective = false
  Rotation = 0
  Scale = 0.5
  ScaleType = 2
  ScrubCount = 0
  SeamHidden = false
  SeamVisible = true
  SmoothHidden = false
  SmoothVisible = true
  Source = -> [Body011]
  X = 195.909
  XDirection = (0.707107,0,-0.707107)
  Y = 92.6714
FEATURE [TechDraw::DrawHatch] Hatch  label="HatchF1"
  HatchPattern = C:/Program Files/FreeCAD 0.21/data/Mod/TechDraw/Patterns/solid.svg
  Source = -> View003 [Face1]
FEATURE [TechDraw::DrawViewBalloon] Balloon013
  BubbleShape = 1
  EndType = 3
  EndTypeScale = 1
  KinkLength = -0.1
  LockPosition = false
  OriginX = -18.2151
  OriginY = -14.1288
  Rotation = 0
  ScaleType = 0
  ShapeScale = 1
  SourceView = -> View003
  TextWrapLen = -1
  X = -91.3723
  Y = -74.5849
FEATURE [TechDraw::DrawViewDimension] Dimension017
  AngleOverride = false
  Arbitrary = false
  ArbitraryTolerances = false
  BoxCorners = (2) [(-52.175,-52.175,0),(52.175,52.175,0)]
  EqualTolerance = true
  ExtensionAngle = 0
  FormatSpec = 2× 4× R%.2w
  FormatSpecOverTolerance = %+.2w
  FormatSpecUnderTolerance = %+.2w
  Inverted = false
  LineAngle = 0
  LockPosition = false
  MeasureType = 1
  OverTolerance = 0
  References2D = -> [View002]
  Rotation = 0
  ScaleType = 0
  TheoreticalExact = false
  Type = 4
  UnderTolerance = 0
  X = 78.9859
  Y = 58.3117
FEATURE [TechDraw::DrawViewDimension] Dimension018
  AngleOverride = false
  Arbitrary = false
  ArbitraryTolerances = false
  BoxCorners = (2) [(-52.175,-52.175,0),(52.175,52.175,0)]
  EqualTolerance = true
  ExtensionAngle = 0
  FormatSpec = ⌀%.2w
  FormatSpecOverTolerance = %+.2w
  FormatSpecUnderTolerance = %+.2w
  Inverted = false
  LineAngle = 0
  LockPosition = false
  MeasureType = 1
  OverTolerance = 0
  References2D = -> [View002]
  Rotation = 0
  ScaleType = 0
  TheoreticalExact = false
  Type = 5
  UnderTolerance = 0
  X = 66.0837
  Y = 9.38895
FEATURE [TechDraw::DrawViewBalloon] Balloon018
  BubbleShape = 6
  EndType = 6
  EndTypeScale = 1
  KinkLength = 0
  LockPosition = false
  OriginX = 66.2827
  OriginY = 1.406
  Rotation = 0
  ScaleType = 0
  ShapeScale = 1
  SourceView = -> Dimension018
  Text = ⌖|⌀ 0,15|A|B|C
  TextWrapLen = -1
  X = 84.6059
  Y = -3.80857
FEATURE [TechDraw::DrawViewPart] View004
  CoarseView = false
  Direction = (0,0,1)
  Focus = 100
  HardHidden = false
  IsoCount = 0
  IsoHidden = false
  IsoVisible = true
  LockPosition = false
  Perspective = false
  Rotation = 0
  ScaleType = 0
  ScrubCount = 0
  SeamHidden = false
  SeamVisible = true
  SmoothHidden = false
  SmoothVisible = true
  Source = -> [Body011]
  X = 148.5
  XDirection = (1,3e-06,0)
  Y = 105
FEATURE [TechDraw::DrawPage] Page002  label="FRONTPANEL-SHEET-VSN2_dxf"
  KeepUpdated = true
  NextBalloonIndex = 1
  ProjectionType = 0
  Template = -> Template002
  Views = -> [View004]
FEATURE [TechDraw::DrawViewDimension] Dimension020
  AngleOverride = false
  Arbitrary = false
  ArbitraryTolerances = false
  BoxCorners = (2) [(-52.175,-52.175,0),(52.175,52.175,0)]
  EqualTolerance = true
  ExtensionAngle = 0
  FormatSpec = 4× 2× R%.2w
  FormatSpecOverTolerance = %+.2w
  FormatSpecUnderTolerance = %+.2w
  Inverted = false
  LineAngle = 0
  LockPosition = false
  MeasureType = 1
  OverTolerance = 0
  References2D = -> [View002]
  Rotation = 0
  ScaleType = 0
  TheoreticalExact = false
  Type = 4
  UnderTolerance = 0
  X = 78.3589
  Y = -15.5904
FEATURE [TechDraw::DrawHatch] Hatch001  label="Hatch001F65"
  HatchPattern = C:/Program Files/FreeCAD 0.21/data/Mod/TechDraw/Patterns/solid.svg
  Source = -> View003 [Face30]
FEATURE [TechDraw::DrawHatch] Hatch002  label="Hatch002F104"
  HatchPattern = C:/Program Files/FreeCAD 0.21/data/Mod/TechDraw/Patterns/solid.svg
  Source = -> View003 [Face32,Face33]
FEATURE [TechDraw::DrawHatch] Hatch003  label="Hatch003F68"
  HatchPattern = C:/Program Files/FreeCAD 0.21/data/Mod/TechDraw/Patterns/solid.svg
  Source = -> View003 [Face34,Face31,Face35]
FEATURE [TechDraw::DrawViewBalloon] Balloon023
  BubbleShape = 1
  EndType = 0
  EndTypeScale = 1
  KinkLength = 7
  LockPosition = false
  OriginX = 44.67
  OriginY = 4.77
  Rotation = 0
  ScaleType = 0
  ShapeScale = 1
  SourceView = -> View002
  Text = 8× 3×6
  TextWrapLen = -1
  X = 80.9138
  Y = -9.03731
FEATURE [TechDraw::DrawViewDimension] Dimension023
  AngleOverride = false
  Arbitrary = false
  ArbitraryTolerances = false
  EqualTolerance = true
  ExtensionAngle = 0
  FormatSpec = %.2w
  FormatSpecOverTolerance = %+.2w
  FormatSpecUnderTolerance = %+.2w
  Inverted = false
  LineAngle = 0
  LockPosition = false
  MeasureType = 1
  OverTolerance = 0
  References2D = -> [ComplexSection]
  Rotation = 0
  ScaleType = 0
  TheoreticalExact = false
  Type = 6
  UnderTolerance = 0
  X = -23.5911
  Y = 26.6553
FEATURE [TechDraw::DrawHatch] Hatch004  label="Hatch004F5"
  HatchPattern = C:/Program Files/FreeCAD 0.21/data/Mod/TechDraw/Patterns/solid.svg
  Source = -> View003 [Face5,Face4]
FEATURE [TechDraw::DrawHatch] Hatch005  label="Hatch005F22"
  HatchPattern = C:/Program Files/FreeCAD 0.21/data/Mod/TechDraw/Patterns/solid.svg
  Source = -> View003 [Face22,Face64,Face118,Face23,Face67,Face65,Face66]
FEATURE [TechDraw::DrawHatch] Hatch006  label="Hatch006F71"
  HatchPattern = C:/Program Files/FreeCAD 0.21/data/Mod/TechDraw/Patterns/solid.svg
  Source = -> View003 [Face71,Face37,Face106,Face50,Face98,Face41,Face68,Face45,Face107,Face103,Face40,Face75,Face39,Face105,Face112]
FEATURE [TechDraw::DrawHatch] Hatch007  label="Hatch007F69"
  HatchPattern = C:/Program Files/FreeCAD 0.21/data/Mod/TechDraw/Patterns/solid.svg
  Source = -> View003 [Face69,Face48,Face46,Face113,Face109,Face51,Face74,Face47,Face110,Face100,Face49,Face44,Face70,Face99,Face108,Face42,Face72,Face38,Face101,Face102,Face43,Face73,Face36,Face111,Edge297]
FEATURE [TechDraw::DrawHatch] Hatch008  label="Hatch008F104"
  HatchPattern = C:/Program Files/FreeCAD 0.21/data/Mod/TechDraw/Patterns/solid.svg
  Source = -> View003 [Face104,Face117,Face27,Face77,Face24,Face116,Face26,Face115,Face25,Face76,Face114]
FEATURE [TechDraw::DrawHatch] Hatch009  label="Hatch009F78"
  HatchPattern = C:/Program Files/FreeCAD 0.21/data/Mod/TechDraw/Patterns/solid.svg
  Source = -> View003 [Face78,Face88,Face125,Face79,Face87,Face126,Face81,Face86,Face130,Face84,Face89,Face128,Face83,Face90,Face127,Face85,Face91,Face129,Face82,Face92,Face123,Face80,Face93,Face124]
FEATURE [TechDraw::DrawViewDimension] Dimension024
  AngleOverride = false
  Arbitrary = false
  ArbitraryTolerances = false
  EqualTolerance = true
  ExtensionAngle = 0
  FormatSpec = 2× %.2w
  FormatSpecOverTolerance = %+.2w
  FormatSpecUnderTolerance = %+.2w
  Inverted = false
  LineAngle = 0
  LockPosition = false
  MeasureType = 1
  OverTolerance = 0
  References2D = -> [View002]
  Rotation = 0
  ScaleType = 0
  TheoreticalExact = false
  Type = 1
  UnderTolerance = 0
  X = 26.4692
  Y = 69.7683
FEATURE [TechDraw::DrawViewDimension] Dimension025
  AngleOverride = false
  Arbitrary = false
  ArbitraryTolerances = false
  EqualTolerance = true
  ExtensionAngle = 0
  FormatSpec = 2× %.2w
  FormatSpecOverTolerance = %+.2w
  FormatSpecUnderTolerance = %+.2w
  Inverted = false
  LineAngle = 0
  LockPosition = false
  MeasureType = 1
  OverTolerance = 0
  References2D = -> [View002]
  Rotation = 0
  ScaleType = 0
  TheoreticalExact = false
  Type = 2
  UnderTolerance = 0
  X = 70.6598
  Y = 27.4654
FEATURE [TechDraw::DrawViewBalloon] Balloon024
  BubbleShape = 6
  EndType = 0
  EndTypeScale = 1
  KinkLength = 5
  LockPosition = false
  OriginX = -26.67
  OriginY = 44.07
  Rotation = 0
  ScaleType = 0
  ShapeScale = 1
  SourceView = -> View
  Text = ⌓|0.2|A|B|C
  TextWrapLen = -1
  X = 18.0244
  Y = 68.2861
FEATURE [TechDraw::DrawViewAnnotation] Annotation004
  Font = osifont
  LineSpace = 100
  LockPosition = false
  MaxWidth = -1
  Rotation = 0
  ScaleType = 0
  Text = 2x
  TextSize = 4
  TextStyle = 0
  X = 119.086
  Y = 276.386
FEATURE [TechDraw::DrawViewDimension] Dimension026
  AngleOverride = false
  Arbitrary = false
  ArbitraryTolerances = true
  EqualTolerance = false
  ExtensionAngle = 0
  FormatSpec = %.2w
  FormatSpecOverTolerance = +0
  FormatSpecUnderTolerance = -0.2
  Inverted = false
  LineAngle = 0
  LockPosition = false
  MeasureType = 1
  OverTolerance = 0
  References2D = -> [View002]
  Rotation = 0
  ScaleType = 0
  TheoreticalExact = false
  Type = 1
  UnderTolerance = 0
  X = 0.708315
  Y = -61.211
FEATURE [TechDraw::DrawViewBalloon] Balloon025
  BubbleShape = 6
  EndType = 6
  EndTypeScale = 1
  KinkLength = 0
  LockPosition = false
  OriginX = 52.1505
  OriginY = -68.4541
  Rotation = 0
  ScaleType = 0
  ShapeScale = 1
  SourceView = -> Dimension026
  Text = B
  TextWrapLen = -1
  X = 62.7295
  Y = -68.5072
FEATURE [TechDraw::DrawViewDimension] Dimension027
  AngleOverride = false
  Arbitrary = false
  ArbitraryTolerances = false
  EqualTolerance = true
  ExtensionAngle = 0
  FormatSpec = 8× %.2w
  FormatSpecOverTolerance = %+.2w
  FormatSpecUnderTolerance = %+.2w
  Inverted = false
  LineAngle = 0
  LockPosition = false
  MeasureType = 1
  OverTolerance = 0
  References2D = -> [View]
  Rotation = 0
  ScaleType = 0
  TheoreticalExact = false
  Type = 1
  UnderTolerance = 0
  X = -17.0519
  Y = -54.5927
FEATURE [TechDraw::DrawViewDimension] Dimension028
  AngleOverride = false
  Arbitrary = false
  ArbitraryTolerances = false
  EqualTolerance = true
  ExtensionAngle = 0
  FormatSpec = 8× %.2w
  FormatSpecOverTolerance = %+.2w
  FormatSpecUnderTolerance = %+.2w
  Inverted = false
  LineAngle = 0
  LockPosition = false
  MeasureType = 1
  OverTolerance = 0
  References2D = -> [View]
  Rotation = 0
  ScaleType = 0
  TheoreticalExact = false
  Type = 2
  UnderTolerance = 0
  X = -61.7485
  Y = -38.005
FEATURE [TechDraw::DrawViewDimension] Dimension029
  AngleOverride = false
  Arbitrary = false
  ArbitraryTolerances = false
  EqualTolerance = true
  ExtensionAngle = 0
  FormatSpec = 8× 4×R%.2w
  FormatSpecOverTolerance = %+.2w
  FormatSpecUnderTolerance = %+.2w
  Inverted = false
  LineAngle = 0
  LockPosition = false
  MeasureType = 1
  OverTolerance = 0
  References2D = -> [View]
  Rotation = 0
  ScaleType = 0
  TheoreticalExact = false
  Type = 4
  UnderTolerance = 0
  X = -76.6534
  Y = -13.9472
FEATURE [TechDraw::DrawViewBalloon] Balloon026
  BubbleShape = 6
  EndType = 0
  EndTypeScale = 1
  KinkLength = 5
  LockPosition = false
  OriginX = -48.355
  OriginY = -13.335
  Rotation = 0
  ScaleType = 0
  ShapeScale = 1
  SourceView = -> View
  Text = ⌓|0.2|A|B|C
  TextWrapLen = -1
  X = -86.491
  Y = 1.83618
FEATURE [TechDraw::DrawViewAnnotation] Annotation005
  Font = osifont
  LineSpace = 100
  LockPosition = false
  MaxWidth = -1
  Rotation = 0
  ScaleType = 0
  Text = 8x
  TextSize = 4
  TextStyle = 0
  X = 16.035
  Y = 211.233
FEATURE [TechDraw::DrawPage] Page  label="VSN2_Drawing"
  KeepUpdated = true
  NextBalloonIndex = 39
  ProjectionType = 0
  Template = -> Template
  Views = -> [View,View001,View002,Dimension,Balloon002,Balloon003,Balloon008,ComplexSection,Dimension008,Dimension009,Balloon012,Dimension010,Annotation,View003,Balloon013,Annotation001,Dimension017,Dimension018,Balloon018,Dimension020,Annotation002,Balloon023,Dimension023,Dimension024,Dimension025,Balloon024,Annotation004,Dimension026,Balloon025,Dimension027,Dimension028,Dimension029,Balloon026,Annotation005,+1 more]
FEATURE [TechDraw::DrawHatch] Hatch010  label="Hatch010F20"
  HatchPattern = C:/Program Files/FreeCAD 0.21/data/Mod/TechDraw/Patterns/solid.svg
  Source = -> View003 [Face20,Face19,Face17,Face15,Face21,Face16,Face18,Face14]
